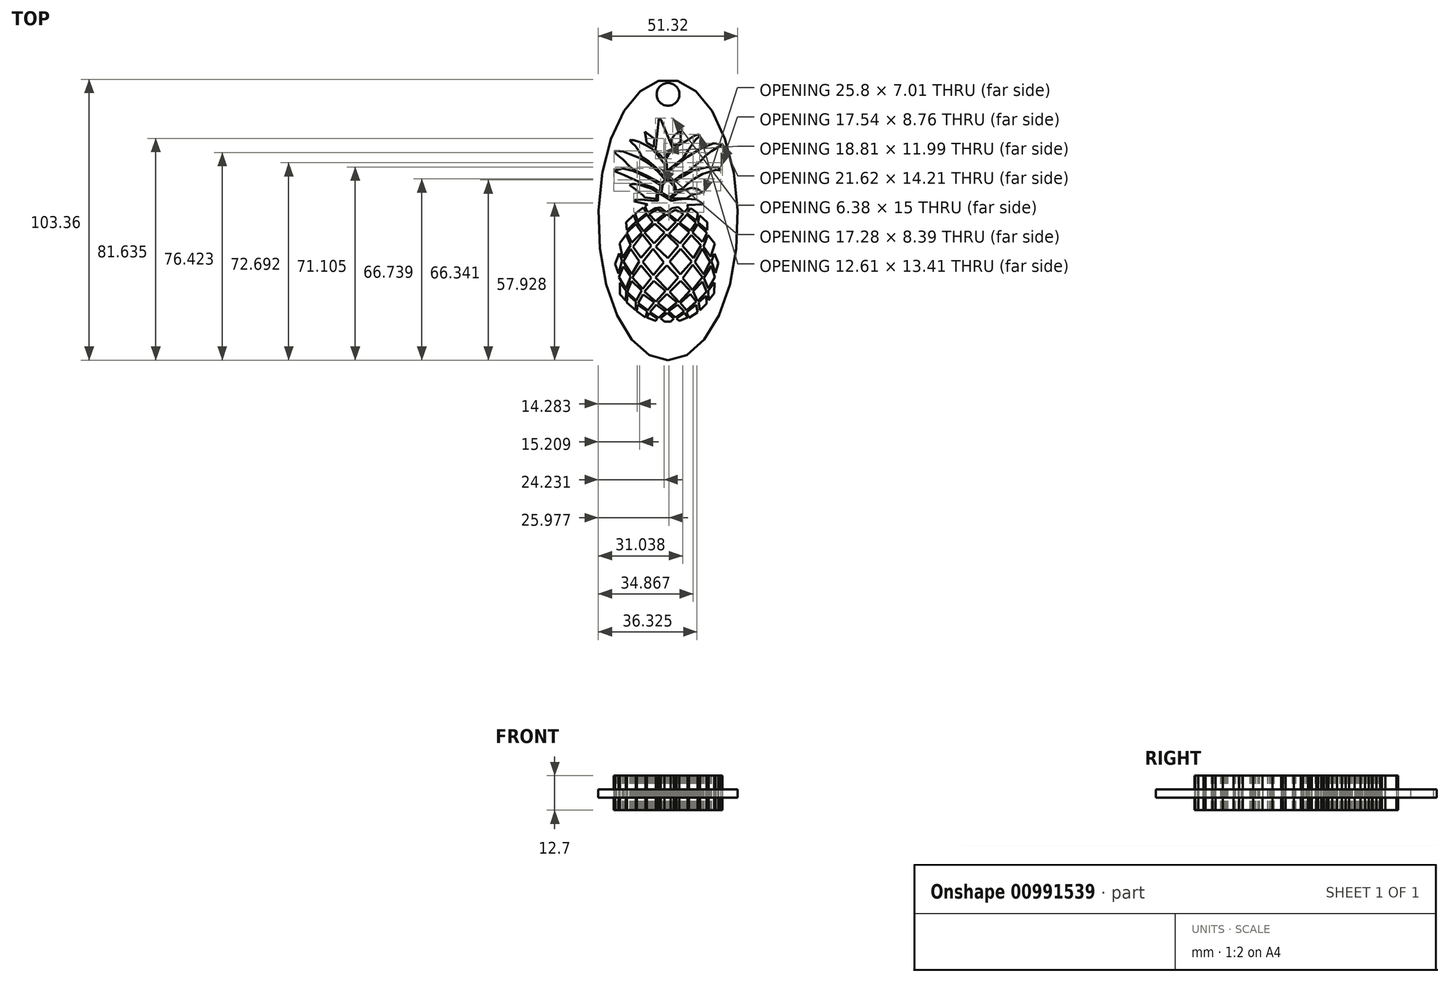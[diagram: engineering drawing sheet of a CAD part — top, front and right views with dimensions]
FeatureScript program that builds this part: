
annotation { "Feature Type Name" : "Feature", "Feature Type Description" : "" }
export const myFeature = defineFeature(function(context is Context, id is Id, definition is map)
    precondition{}
    {
        {
            var Q0;
            Q0=qCreatedBy(makeId("Top.planeOp"),FACE);
            var sketch = newSketch(context, id + "F0", { "sketchPlane" : qUnion([Q0])});
            skLineSegment(sketch, "E0", {"start": v(-25.66, -1.5) * mm, "end": v(-25.25, -6.5) * mm});
            skLineSegment(sketch, "E1", {"start": v(-25.25, -6.5) * mm, "end": v(-19.48, -1.16) * mm});
            skLineSegment(sketch, "E2", {"start": v(-19.48, -1.16) * mm, "end": v(-21, 2.9) * mm});
            skLineSegment(sketch, "E3", {"start": v(-21, 2.9) * mm, "end": v(-25.66, -1.5) * mm});
            skLineSegment(sketch, "E4", {"start": v(-20.22, 3.8) * mm, "end": v(-18.77, -0.42) * mm});
            skLineSegment(sketch, "E5", {"start": v(-18.77, -0.42) * mm, "end": v(-13.06, 4.15) * mm});
            skLineSegment(sketch, "E6", {"start": v(-13.06, 4.15) * mm, "end": v(-15.05, 7.52) * mm});
            skLineSegment(sketch, "E7", {"start": v(-15.05, 7.52) * mm, "end": v(-20.22, 3.8) * mm});
            skLineSegment(sketch, "E8", {"start": v(-18.89, -1.52) * mm, "end": v(-14.98, -7.06) * mm});
            skLineSegment(sketch, "E9", {"start": v(-14.98, -7.06) * mm, "end": v(-9.4, -1.52) * mm});
            skLineSegment(sketch, "E10", {"start": v(-9.4, -1.52) * mm, "end": v(-13.06, 3.14) * mm});
            skLineSegment(sketch, "E11", {"start": v(-13.06, 3.14) * mm, "end": v(-18.89, -1.52) * mm});
            skLineSegment(sketch, "E12", {"start": v(-25.2, -7.88) * mm, "end": v(-22.35, -14.06) * mm});
            skLineSegment(sketch, "E13", {"start": v(-22.35, -14.06) * mm, "end": v(-16.27, -7.88) * mm});
            skLineSegment(sketch, "E14", {"start": v(-16.27, -7.88) * mm, "end": v(-19.8, -2.51) * mm});
            skLineSegment(sketch, "E15", {"start": v(-19.8, -2.51) * mm, "end": v(-25.2, -7.88) * mm});
            skLineSegment(sketch, "E16", {"start": v(-25.66, -9.17) * mm, "end": v(-29.74, -14.43) * mm});
            skLineSegment(sketch, "E17", {"start": v(-29.74, -14.43) * mm, "end": v(-27.7, -23.26) * mm});
            skLineSegment(sketch, "E18", {"start": v(-27.7, -23.26) * mm, "end": v(-22.9, -15.5) * mm});
            skLineSegment(sketch, "E19", {"start": v(-22.9, -15.5) * mm, "end": v(-25.66, -9.17) * mm});
            skLineSegment(sketch, "E20", {"start": v(-21.48, -16.47) * mm, "end": v(-16.64, -23.26) * mm});
            skLineSegment(sketch, "E21", {"start": v(-16.64, -23.26) * mm, "end": v(-10.19, -16.03) * mm});
            skLineSegment(sketch, "E22", {"start": v(-10.19, -16.03) * mm, "end": v(-15.65, -8.87) * mm});
            skLineSegment(sketch, "E23", {"start": v(-15.65, -8.87) * mm, "end": v(-21.48, -16.47) * mm});
            skLineSegment(sketch, "E24", {"start": v(-30, -20.49) * mm, "end": v(-32.38, -27.19) * mm});
            skLineSegment(sketch, "E25", {"start": v(-32.38, -27.19) * mm, "end": v(-30.27, -33.09) * mm});
            skLineSegment(sketch, "E26", {"start": v(-30.27, -33.09) * mm, "end": v(-28.16, -24.99) * mm});
            skLineSegment(sketch, "E27", {"start": v(-28.16, -24.99) * mm, "end": v(-30, -20.49) * mm});
            skLineSegment(sketch, "E28", {"start": v(-27.43, -25.7) * mm, "end": v(-22.9, -17.8) * mm});
            skLineSegment(sketch, "E29", {"start": v(-22.9, -17.8) * mm, "end": v(-17.62, -25.44) * mm});
            skLineSegment(sketch, "E30", {"start": v(-17.62, -25.44) * mm, "end": v(-22.3, -33.55) * mm});
            skLineSegment(sketch, "E31", {"start": v(-22.3, -33.55) * mm, "end": v(-27.43, -25.7) * mm});
            skLineSegment(sketch, "E32", {"start": v(-29.58, -38.67) * mm, "end": v(-25.77, -43.74) * mm});
            skLineSegment(sketch, "E33", {"start": v(-25.77, -43.74) * mm, "end": v(-25.9, -49.5) * mm});
            skLineSegment(sketch, "E34", {"start": v(-25.9, -49.5) * mm, "end": v(-29.58, -45.83) * mm});
            skLineSegment(sketch, "E35", {"start": v(-29.58, -45.83) * mm, "end": v(-29.58, -38.67) * mm});
            skLineSegment(sketch, "E36", {"start": v(-25.89, -42.39) * mm, "end": v(-22.9, -35.09) * mm});
            skLineSegment(sketch, "E37", {"start": v(-22.9, -35.09) * mm, "end": v(-27.43, -28.61) * mm});
            skLineSegment(sketch, "E38", {"start": v(-27.43, -28.61) * mm, "end": v(-30.13, -35.18) * mm});
            skLineSegment(sketch, "E39", {"start": v(-30.13, -35.18) * mm, "end": v(-25.89, -42.39) * mm});
            skLineSegment(sketch, "E40", {"start": v(-25.06, -44.25) * mm, "end": v(-22.28, -37.5) * mm});
            skLineSegment(sketch, "E41", {"start": v(-22.28, -37.5) * mm, "end": v(-16.15, -43.49) * mm});
            skLineSegment(sketch, "E42", {"start": v(-16.15, -43.49) * mm, "end": v(-19.57, -49.5) * mm});
            skLineSegment(sketch, "E43", {"start": v(-19.57, -49.5) * mm, "end": v(-25.06, -44.25) * mm});
            skLineSegment(sketch, "E44", {"start": v(-24.8, -45.83) * mm, "end": v(-19.76, -50.26) * mm});
            skLineSegment(sketch, "E45", {"start": v(-19.76, -50.26) * mm, "end": v(-19.76, -55.47) * mm});
            skLineSegment(sketch, "E46", {"start": v(-19.76, -55.47) * mm, "end": v(-25.36, -50.95) * mm});
            skLineSegment(sketch, "E47", {"start": v(-25.36, -50.95) * mm, "end": v(-24.8, -45.83) * mm});
            skLineSegment(sketch, "E48", {"start": v(-19.16, -56.23) * mm, "end": v(-18.61, -52.19) * mm});
            skLineSegment(sketch, "E49", {"start": v(-18.61, -52.19) * mm, "end": v(-12.83, -56.23) * mm});
            skLineSegment(sketch, "E50", {"start": v(-12.83, -56.23) * mm, "end": v(-13.84, -60) * mm});
            skLineSegment(sketch, "E51", {"start": v(-13.84, -60) * mm, "end": v(-19.16, -56.23) * mm});
            skLineSegment(sketch, "E52", {"start": v(-11.6, -57.29) * mm, "end": v(-6.67, -60.45) * mm});
            skLineSegment(sketch, "E53", {"start": v(-6.67, -60.45) * mm, "end": v(-7.6, -62.06) * mm});
            skLineSegment(sketch, "E54", {"start": v(-7.6, -62.06) * mm, "end": v(-12.92, -60) * mm});
            skLineSegment(sketch, "E55", {"start": v(-12.92, -60) * mm, "end": v(-11.6, -57.29) * mm});
            skLineSegment(sketch, "E56", {"start": v(-2.29, -62.43) * mm, "end": v(1.52, -62.43) * mm});
            skLineSegment(sketch, "E57", {"start": v(1.52, -62.43) * mm, "end": v(3.43, -60.6) * mm});
            skLineSegment(sketch, "E58", {"start": v(3.43, -60.6) * mm, "end": v(-0.54, -57.17) * mm});
            skLineSegment(sketch, "E59", {"start": v(-0.54, -57.17) * mm, "end": v(-4.5, -60.45) * mm});
            skLineSegment(sketch, "E60", {"start": v(-4.5, -60.45) * mm, "end": v(-2.29, -62.43) * mm});
            skLineSegment(sketch, "E61", {"start": v(-5.7, -60.25) * mm, "end": v(-1.49, -56.3) * mm});
            skLineSegment(sketch, "E62", {"start": v(-1.49, -56.3) * mm, "end": v(-7.34, -52.19) * mm});
            skLineSegment(sketch, "E63", {"start": v(-7.34, -52.19) * mm, "end": v(-11.06, -56.55) * mm});
            skLineSegment(sketch, "E64", {"start": v(-11.06, -56.55) * mm, "end": v(-5.7, -60.25) * mm});
            skLineSegment(sketch, "E65", {"start": v(6.85, -62.06) * mm, "end": v(11.9, -60) * mm});
            skLineSegment(sketch, "E66", {"start": v(11.9, -60) * mm, "end": v(10.08, -57.17) * mm});
            skLineSegment(sketch, "E67", {"start": v(10.08, -57.17) * mm, "end": v(5.15, -60.68) * mm});
            skLineSegment(sketch, "E68", {"start": v(5.15, -60.68) * mm, "end": v(6.85, -62.06) * mm});
            skLineSegment(sketch, "E69", {"start": v(4.67, -60) * mm, "end": v(9.8, -56.22) * mm});
            skLineSegment(sketch, "E70", {"start": v(9.8, -56.22) * mm, "end": v(5.95, -52.19) * mm});
            skLineSegment(sketch, "E71", {"start": v(0.4, -56.22) * mm, "end": v(4.67, -60) * mm});
            skLineSegment(sketch, "E72", {"start": v(12.93, -60.09) * mm, "end": v(18.23, -56.83) * mm});
            skLineSegment(sketch, "E73", {"start": v(18.23, -56.83) * mm, "end": v(17.22, -52.19) * mm});
            skLineSegment(sketch, "E74", {"start": v(17.22, -52.19) * mm, "end": v(11.26, -56.78) * mm});
            skLineSegment(sketch, "E75", {"start": v(11.26, -56.78) * mm, "end": v(12.93, -60.09) * mm});
            skLineSegment(sketch, "E76", {"start": v(19.52, -55.6) * mm, "end": v(23.67, -51.43) * mm});
            skLineSegment(sketch, "E77", {"start": v(23.67, -51.43) * mm, "end": v(23.5, -46.61) * mm});
            skLineSegment(sketch, "E78", {"start": v(23.5, -46.61) * mm, "end": v(18.83, -50.6) * mm});
            skLineSegment(sketch, "E79", {"start": v(18.83, -50.6) * mm, "end": v(19.52, -55.6) * mm});
            skLineSegment(sketch, "E80", {"start": v(24.87, -49.48) * mm, "end": v(28.22, -45.16) * mm});
            skLineSegment(sketch, "E81", {"start": v(28.22, -45.16) * mm, "end": v(28.52, -38.53) * mm});
            skLineSegment(sketch, "E82", {"start": v(28.52, -38.53) * mm, "end": v(24.7, -43.42) * mm});
            skLineSegment(sketch, "E83", {"start": v(24.7, -43.42) * mm, "end": v(24.87, -49.48) * mm});
            skLineSegment(sketch, "E84", {"start": v(24.7, -42.23) * mm, "end": v(28.81, -35.16) * mm});
            skLineSegment(sketch, "E85", {"start": v(28.81, -35.16) * mm, "end": v(26.61, -28.25) * mm});
            skLineSegment(sketch, "E86", {"start": v(26.61, -28.25) * mm, "end": v(21.88, -35.61) * mm});
            skLineSegment(sketch, "E87", {"start": v(21.88, -35.61) * mm, "end": v(24.7, -42.23) * mm});
            skLineSegment(sketch, "E88", {"start": v(29.1, -32.7) * mm, "end": v(30.74, -26.55) * mm});
            skLineSegment(sketch, "E89", {"start": v(30.74, -26.55) * mm, "end": v(28.5, -20.78) * mm});
            skLineSegment(sketch, "E90", {"start": v(28.5, -20.78) * mm, "end": v(26.59, -25.37) * mm});
            skLineSegment(sketch, "E91", {"start": v(26.59, -25.37) * mm, "end": v(29.1, -32.7) * mm});
            skLineSegment(sketch, "E92", {"start": v(26.08, -22.69) * mm, "end": v(28.81, -14.65) * mm});
            skLineSegment(sketch, "E93", {"start": v(28.81, -14.65) * mm, "end": v(24.54, -9.28) * mm});
            skLineSegment(sketch, "E94", {"start": v(24.54, -9.28) * mm, "end": v(21.68, -16.37) * mm});
            skLineSegment(sketch, "E95", {"start": v(21.68, -16.37) * mm, "end": v(26.08, -22.69) * mm});
            skLineSegment(sketch, "E96", {"start": v(20.99, -13.69) * mm, "end": v(23.83, -8.2) * mm});
            skLineSegment(sketch, "E97", {"start": v(23.83, -8.2) * mm, "end": v(18.2, -2.6) * mm});
            skLineSegment(sketch, "E98", {"start": v(18.2, -2.6) * mm, "end": v(14.88, -7.74) * mm});
            skLineSegment(sketch, "E99", {"start": v(14.88, -7.74) * mm, "end": v(20.99, -13.69) * mm});
            skLineSegment(sketch, "E100", {"start": v(24.02, -6.48) * mm, "end": v(24.02, -1.54) * mm});
            skLineSegment(sketch, "E101", {"start": v(24.02, -1.54) * mm, "end": v(19.36, 2.68) * mm});
            skLineSegment(sketch, "E102", {"start": v(19.36, 2.68) * mm, "end": v(18.28, -1.59) * mm});
            skLineSegment(sketch, "E103", {"start": v(18.28, -1.59) * mm, "end": v(24.02, -6.48) * mm});
            skLineSegment(sketch, "E104", {"start": v(11.46, 3.92) * mm, "end": v(13.8, 7.2) * mm});
            skLineSegment(sketch, "E105", {"start": v(13.8, 7.2) * mm, "end": v(18.28, 3.92) * mm});
            skLineSegment(sketch, "E106", {"start": v(18.28, 3.92) * mm, "end": v(17.48, -0.47) * mm});
            skLineSegment(sketch, "E107", {"start": v(17.48, -0.47) * mm, "end": v(11.46, 3.92) * mm});
            skLineSegment(sketch, "E108", {"start": v(5.77, -0.72) * mm, "end": v(9.53, 3.67) * mm});
            skLineSegment(sketch, "E109", {"start": v(9.53, 3.67) * mm, "end": v(4.63, 6.14) * mm});
            skLineSegment(sketch, "E110", {"start": v(4.63, 6.14) * mm, "end": v(0.21, 3.76) * mm});
            skLineSegment(sketch, "E111", {"start": v(0.21, 3.76) * mm, "end": v(5.77, -0.72) * mm});
            skLineSegment(sketch, "E112", {"start": v(7.17, -1.68) * mm, "end": v(13.64, -6.64) * mm});
            skLineSegment(sketch, "E113", {"start": v(13.64, -6.64) * mm, "end": v(16.97, -1.68) * mm});
            skLineSegment(sketch, "E114", {"start": v(16.97, -1.68) * mm, "end": v(11.46, 3.12) * mm});
            skLineSegment(sketch, "E115", {"start": v(11.46, 3.12) * mm, "end": v(7.17, -1.68) * mm});
            skLineSegment(sketch, "E116", {"start": v(-11.65, 3.55) * mm, "end": v(-6.31, 6.44) * mm});
            skLineSegment(sketch, "E117", {"start": v(-6.31, 6.44) * mm, "end": v(-2.07, 3.81) * mm});
            skLineSegment(sketch, "E118", {"start": v(-2.07, 3.81) * mm, "end": v(-7.74, -0.72) * mm});
            skLineSegment(sketch, "E119", {"start": v(-7.74, -0.72) * mm, "end": v(-11.65, 3.55) * mm});
            skLineSegment(sketch, "E120", {"start": v(-14.43, -7.97) * mm, "end": v(-8.05, -2.34) * mm});
            skLineSegment(sketch, "E121", {"start": v(-8.05, -2.34) * mm, "end": v(-2.26, -7.97) * mm});
            skLineSegment(sketch, "E122", {"start": v(-2.26, -7.97) * mm, "end": v(-8.44, -14.46) * mm});
            skLineSegment(sketch, "E123", {"start": v(-8.44, -14.46) * mm, "end": v(-14.43, -7.97) * mm});
            skLineSegment(sketch, "E124", {"start": v(-6.53, -1.28) * mm, "end": v(-0.6, -6.64) * mm});
            skLineSegment(sketch, "E125", {"start": v(-0.6, -6.64) * mm, "end": v(4.87, -1.4) * mm});
            skLineSegment(sketch, "E126", {"start": v(4.87, -1.4) * mm, "end": v(-0.73, 3.37) * mm});
            skLineSegment(sketch, "E127", {"start": v(-0.73, 3.37) * mm, "end": v(-6.53, -1.28) * mm});
            skLineSegment(sketch, "E128", {"start": v(0.58, -8.69) * mm, "end": v(7.43, -14.46) * mm});
            skLineSegment(sketch, "E129", {"start": v(7.43, -14.46) * mm, "end": v(13.07, -7.72) * mm});
            skLineSegment(sketch, "E130", {"start": v(13.07, -7.72) * mm, "end": v(6.52, -2.19) * mm});
            skLineSegment(sketch, "E131", {"start": v(6.52, -2.19) * mm, "end": v(0.58, -8.69) * mm});
            skLineSegment(sketch, "E132", {"start": v(-7.39, -16.48) * mm, "end": v(-0.83, -8.87) * mm});
            skLineSegment(sketch, "E133", {"start": v(-0.83, -8.87) * mm, "end": v(6.37, -15.98) * mm});
            skLineSegment(sketch, "E134", {"start": v(6.37, -15.98) * mm, "end": v(0.02, -23.62) * mm});
            skLineSegment(sketch, "E135", {"start": v(0.02, -23.62) * mm, "end": v(-7.39, -16.48) * mm});
            skLineSegment(sketch, "E136", {"start": v(8.75, -15.98) * mm, "end": v(14.4, -9.28) * mm});
            skLineSegment(sketch, "E137", {"start": v(14.4, -9.28) * mm, "end": v(20.16, -15.77) * mm});
            skLineSegment(sketch, "E138", {"start": v(20.16, -15.77) * mm, "end": v(15.51, -23.62) * mm});
            skLineSegment(sketch, "E139", {"start": v(15.51, -23.62) * mm, "end": v(8.75, -15.98) * mm});
            skLineSegment(sketch, "E140", {"start": v(16.38, -25.9) * mm, "end": v(21.15, -17.57) * mm});
            skLineSegment(sketch, "E141", {"start": v(21.15, -17.57) * mm, "end": v(25.73, -25.67) * mm});
            skLineSegment(sketch, "E142", {"start": v(25.73, -25.67) * mm, "end": v(21.88, -33.55) * mm});
            skLineSegment(sketch, "E143", {"start": v(21.88, -33.55) * mm, "end": v(16.38, -25.9) * mm});
            skLineSegment(sketch, "E144", {"start": v(7.56, -33.55) * mm, "end": v(14.46, -25.67) * mm});
            skLineSegment(sketch, "E145", {"start": v(14.46, -25.67) * mm, "end": v(7.74, -17.8) * mm});
            skLineSegment(sketch, "E146", {"start": v(7.74, -17.8) * mm, "end": v(0.95, -25.67) * mm});
            skLineSegment(sketch, "E147", {"start": v(0.95, -25.67) * mm, "end": v(7.56, -33.55) * mm});
            skLineSegment(sketch, "E148", {"start": v(8.97, -35.82) * mm, "end": v(15.15, -27.62) * mm});
            skLineSegment(sketch, "E149", {"start": v(15.15, -27.62) * mm, "end": v(21.06, -35.24) * mm});
            skLineSegment(sketch, "E150", {"start": v(21.06, -35.24) * mm, "end": v(14.88, -43.05) * mm});
            skLineSegment(sketch, "E151", {"start": v(14.88, -43.05) * mm, "end": v(8.97, -35.82) * mm});
            skLineSegment(sketch, "E152", {"start": v(-8.93, -33.88) * mm, "end": v(-2.54, -26.12) * mm});
            skLineSegment(sketch, "E153", {"start": v(-2.54, -26.12) * mm, "end": v(-9.24, -17.8) * mm});
            skLineSegment(sketch, "E154", {"start": v(-9.24, -17.8) * mm, "end": v(-15.59, -25.84) * mm});
            skLineSegment(sketch, "E155", {"start": v(-15.59, -25.84) * mm, "end": v(-8.93, -33.88) * mm});
            skLineSegment(sketch, "E156", {"start": v(-21.8, -35.5) * mm, "end": v(-16.7, -27.93) * mm});
            skLineSegment(sketch, "E157", {"start": v(-16.7, -27.93) * mm, "end": v(-10.19, -35.65) * mm});
            skLineSegment(sketch, "E158", {"start": v(-10.19, -35.65) * mm, "end": v(-15.59, -42.39) * mm});
            skLineSegment(sketch, "E159", {"start": v(-15.59, -42.39) * mm, "end": v(-21.8, -35.5) * mm});
            skLineSegment(sketch, "E160", {"start": v(-7.65, -35.5) * mm, "end": v(-0.2, -43.05) * mm});
            skLineSegment(sketch, "E161", {"start": v(-0.2, -43.05) * mm, "end": v(6.37, -35.5) * mm});
            skLineSegment(sketch, "E162", {"start": v(6.37, -35.5) * mm, "end": v(-0.64, -27.93) * mm});
            skLineSegment(sketch, "E163", {"start": v(-14.49, -44.08) * mm, "end": v(-8.75, -37.5) * mm});
            skLineSegment(sketch, "E164", {"start": v(-8.75, -37.5) * mm, "end": v(-1.49, -43.71) * mm});
            skLineSegment(sketch, "E165", {"start": v(-1.49, -43.71) * mm, "end": v(-7.39, -50.2) * mm});
            skLineSegment(sketch, "E166", {"start": v(-7.39, -50.2) * mm, "end": v(-14.49, -44.08) * mm});
            skLineSegment(sketch, "E167", {"start": v(-18.32, -51.11) * mm, "end": v(-15.37, -45.83) * mm});
            skLineSegment(sketch, "E168", {"start": v(-15.37, -45.83) * mm, "end": v(-8.49, -50.65) * mm});
            skLineSegment(sketch, "E169", {"start": v(-8.49, -50.65) * mm, "end": v(-12.41, -55.6) * mm});
            skLineSegment(sketch, "E170", {"start": v(-12.41, -55.6) * mm, "end": v(-18.32, -51.11) * mm});
            skLineSegment(sketch, "E171", {"start": v(-6.27, -51.11) * mm, "end": v(-0.64, -45.48) * mm});
            skLineSegment(sketch, "E172", {"start": v(-0.64, -45.48) * mm, "end": v(5.45, -50.72) * mm});
            skLineSegment(sketch, "E173", {"start": v(5.45, -50.72) * mm, "end": v(-0.41, -55.6) * mm});
            skLineSegment(sketch, "E174", {"start": v(-0.41, -55.6) * mm, "end": v(-6.27, -51.11) * mm});
            skLineSegment(sketch, "E175", {"start": v(0.95, -44.29) * mm, "end": v(7.7, -37.5) * mm});
            skLineSegment(sketch, "E176", {"start": v(7.7, -37.5) * mm, "end": v(13.43, -43.5) * mm});
            skLineSegment(sketch, "E177", {"start": v(13.43, -43.5) * mm, "end": v(6.95, -50.54) * mm});
            skLineSegment(sketch, "E178", {"start": v(6.95, -50.54) * mm, "end": v(0.95, -44.29) * mm});
            skLineSegment(sketch, "E179", {"start": v(7.47, -51.11) * mm, "end": v(13.7, -45.48) * mm});
            skLineSegment(sketch, "E180", {"start": v(13.7, -45.48) * mm, "end": v(17.35, -50.2) * mm});
            skLineSegment(sketch, "E181", {"start": v(17.35, -50.2) * mm, "end": v(11.26, -55.6) * mm});
            skLineSegment(sketch, "E182", {"start": v(11.26, -55.6) * mm, "end": v(7.47, -51.11) * mm});
            skLineSegment(sketch, "E183", {"start": v(15.32, -43.85) * mm, "end": v(18.23, -49.93) * mm});
            skLineSegment(sketch, "E184", {"start": v(18.23, -49.93) * mm, "end": v(23.67, -44.08) * mm});
            skLineSegment(sketch, "E185", {"start": v(23.67, -44.08) * mm, "end": v(21.06, -37.85) * mm});
            skLineSegment(sketch, "E186", {"start": v(21.06, -37.85) * mm, "end": v(15.32, -43.85) * mm});
            skLineSegment(sketch, "E187", {"start": v(-0.83, 4.57) * mm, "end": v(2.5, 7.2) * mm});
            skLineSegment(sketch, "E188", {"start": v(2.5, 7.2) * mm, "end": v(6.37, 7.8) * mm});
            skLineSegment(sketch, "E189", {"start": v(6.37, 7.8) * mm, "end": v(9.9, 4.57) * mm});
            skLineSegment(sketch, "E190", {"start": v(9.9, 4.57) * mm, "end": v(11.62, 6.2) * mm});
            skLineSegment(sketch, "E191", {"start": v(11.62, 6.2) * mm, "end": v(12.33, 7.83) * mm});
            skLineSegment(sketch, "E192", {"start": v(12.33, 7.83) * mm, "end": v(11.46, 9.03) * mm});
            skLineSegment(sketch, "E193", {"start": v(11.46, 9.03) * mm, "end": v(22.03, 9.55) * mm});
            skLineSegment(sketch, "E194", {"start": v(22.03, 9.55) * mm, "end": v(17.4, 12.38) * mm});
            skLineSegment(sketch, "E195", {"start": v(17.4, 12.38) * mm, "end": v(11, 12.77) * mm});
            skLineSegment(sketch, "E196", {"start": v(11, 12.77) * mm, "end": v(6.02, 12.42) * mm});
            skLineSegment(sketch, "E197", {"start": v(6.02, 12.42) * mm, "end": v(2.27, 11.63) * mm});
            skLineSegment(sketch, "E198", {"start": v(2.27, 11.63) * mm, "end": v(-5.18, 16.26) * mm});
            skLineSegment(sketch, "E199", {"start": v(-5.18, 16.26) * mm, "end": v(-6.15, 15.07) * mm});
            skLineSegment(sketch, "E200", {"start": v(-6.15, 15.07) * mm, "end": v(-6.15, 11.58) * mm});
            skLineSegment(sketch, "E201", {"start": v(-6.15, 11.58) * mm, "end": v(-10.37, 11.86) * mm});
            skLineSegment(sketch, "E202", {"start": v(-10.37, 11.86) * mm, "end": v(-16.64, 12.47) * mm});
            skLineSegment(sketch, "E203", {"start": v(-16.64, 12.47) * mm, "end": v(-20.48, 12.16) * mm});
            skLineSegment(sketch, "E204", {"start": v(-20.48, 12.16) * mm, "end": v(-20.97, 11.4) * mm});
            skLineSegment(sketch, "E205", {"start": v(-20.97, 11.4) * mm, "end": v(-12.59, 9.51) * mm});
            skLineSegment(sketch, "E206", {"start": v(-12.59, 9.51) * mm, "end": v(-14.15, 8.1) * mm});
            skLineSegment(sketch, "E207", {"start": v(-14.15, 8.1) * mm, "end": v(-13.25, 5.8) * mm});
            skLineSegment(sketch, "E208", {"start": v(-13.25, 5.8) * mm, "end": v(-11.65, 4.57) * mm});
            skLineSegment(sketch, "E209", {"start": v(-11.65, 4.57) * mm, "end": v(-7.78, 7.2) * mm});
            skLineSegment(sketch, "E210", {"start": v(-7.78, 7.2) * mm, "end": v(-4.65, 7.52) * mm});
            skLineSegment(sketch, "E211", {"start": v(-4.65, 7.52) * mm, "end": v(-0.83, 4.57) * mm});
            skLineSegment(sketch, "E212", {"start": v(1.74, 13.08) * mm, "end": v(11.46, 13.3) * mm});
            skLineSegment(sketch, "E213", {"start": v(11.46, 13.3) * mm, "end": v(14.46, 15.33) * mm});
            skLineSegment(sketch, "E214", {"start": v(14.46, 15.33) * mm, "end": v(19.36, 16.26) * mm});
            skLineSegment(sketch, "E215", {"start": v(19.36, 16.26) * mm, "end": v(21.15, 16.87) * mm});
            skLineSegment(sketch, "E216", {"start": v(21.15, 16.87) * mm, "end": v(18.28, 18.73) * mm});
            skLineSegment(sketch, "E217", {"start": v(18.28, 18.73) * mm, "end": v(14.46, 19.65) * mm});
            skLineSegment(sketch, "E218", {"start": v(14.46, 19.65) * mm, "end": v(9.63, 18.18) * mm});
            skLineSegment(sketch, "E219", {"start": v(9.63, 18.18) * mm, "end": v(6.1, 16.66) * mm});
            skLineSegment(sketch, "E220", {"start": v(6.1, 16.66) * mm, "end": v(1.74, 13.08) * mm});
            skLineSegment(sketch, "E221", {"start": v(-23.48, 21.37) * mm, "end": v(-19.48, 18.33) * mm});
            skLineSegment(sketch, "E222", {"start": v(-19.48, 18.33) * mm, "end": v(-15.37, 14.98) * mm});
            skLineSegment(sketch, "E223", {"start": v(-15.37, 14.98) * mm, "end": v(-14.21, 13.6) * mm});
            skLineSegment(sketch, "E224", {"start": v(-14.21, 13.6) * mm, "end": v(-7.17, 12.86) * mm});
            skLineSegment(sketch, "E225", {"start": v(-7.17, 12.86) * mm, "end": v(-7.17, 14.85) * mm});
            skLineSegment(sketch, "E226", {"start": v(-7.17, 14.85) * mm, "end": v(-6.53, 16.79) * mm});
            skLineSegment(sketch, "E227", {"start": v(-6.53, 16.79) * mm, "end": v(-9.74, 19) * mm});
            skLineSegment(sketch, "E228", {"start": v(-9.74, 19) * mm, "end": v(-19.12, 22) * mm});
            skLineSegment(sketch, "E229", {"start": v(-19.12, 22) * mm, "end": v(-21.98, 22) * mm});
            skLineSegment(sketch, "E230", {"start": v(-21.98, 22) * mm, "end": v(-23.48, 21.37) * mm});
            skLineSegment(sketch, "E231", {"start": v(-4.08, 16.61) * mm, "end": v(0.95, 13.79) * mm});
            skLineSegment(sketch, "E232", {"start": v(0.95, 13.79) * mm, "end": v(4.65, 16.96) * mm});
            skLineSegment(sketch, "E233", {"start": v(4.65, 16.96) * mm, "end": v(3.6, 20.78) * mm});
            skLineSegment(sketch, "E234", {"start": v(3.6, 20.78) * mm, "end": v(-0.1, 24.61) * mm});
            skLineSegment(sketch, "E235", {"start": v(-0.1, 24.61) * mm, "end": v(-3.27, 21.5) * mm});
            skLineSegment(sketch, "E236", {"start": v(-3.27, 21.5) * mm, "end": v(-4.08, 16.61) * mm});
            skLineSegment(sketch, "E237", {"start": v(-33.36, 29.93) * mm, "end": v(-26.88, 27.46) * mm});
            skLineSegment(sketch, "E238", {"start": v(-26.88, 27.46) * mm, "end": v(-21.85, 25.2) * mm});
            skLineSegment(sketch, "E239", {"start": v(-21.85, 25.2) * mm, "end": v(-17, 22.92) * mm});
            skLineSegment(sketch, "E240", {"start": v(-17, 22.92) * mm, "end": v(-15, 21.64) * mm});
            skLineSegment(sketch, "E241", {"start": v(-11.65, 20.71) * mm, "end": v(-8.8, 19.65) * mm});
            skLineSegment(sketch, "E242", {"start": v(-8.8, 19.65) * mm, "end": v(-6.86, 18.42) * mm});
            skLineSegment(sketch, "E243", {"start": v(-6.86, 18.42) * mm, "end": v(-6.33, 17.44) * mm});
            skLineSegment(sketch, "E244", {"start": v(-6.33, 17.44) * mm, "end": v(-4.96, 17.44) * mm});
            skLineSegment(sketch, "E245", {"start": v(-4.96, 17.44) * mm, "end": v(-4.65, 20.05) * mm});
            skLineSegment(sketch, "E246", {"start": v(-4.65, 20.05) * mm, "end": v(-4.56, 21.36) * mm});
            skLineSegment(sketch, "E247", {"start": v(-4.56, 21.36) * mm, "end": v(-7.65, 23.31) * mm});
            skLineSegment(sketch, "E248", {"start": v(-7.65, 23.31) * mm, "end": v(-14.15, 26.58) * mm});
            skLineSegment(sketch, "E249", {"start": v(-14.15, 26.58) * mm, "end": v(-21.5, 29.93) * mm});
            skLineSegment(sketch, "E250", {"start": v(-21.5, 29.93) * mm, "end": v(-27.76, 31.43) * mm});
            skLineSegment(sketch, "E251", {"start": v(-27.76, 31.43) * mm, "end": v(-33.36, 29.93) * mm});
            skLineSegment(sketch, "E252", {"start": v(5.14, 17.8) * mm, "end": v(9.06, 19.26) * mm});
            skLineSegment(sketch, "E253", {"start": v(9.06, 19.26) * mm, "end": v(11.7, 22.02) * mm});
            skLineSegment(sketch, "E254", {"start": v(11.7, 22.02) * mm, "end": v(16.03, 25.08) * mm});
            skLineSegment(sketch, "E255", {"start": v(16.03, 25.08) * mm, "end": v(21.15, 27.99) * mm});
            skLineSegment(sketch, "E256", {"start": v(21.15, 27.99) * mm, "end": v(29.3, 30.68) * mm});
            skLineSegment(sketch, "E257", {"start": v(29.3, 30.68) * mm, "end": v(32.39, 30.24) * mm});
            skLineSegment(sketch, "E258", {"start": v(32.39, 30.24) * mm, "end": v(30.93, 32.4) * mm});
            skLineSegment(sketch, "E259", {"start": v(30.93, 32.4) * mm, "end": v(23.13, 32.04) * mm});
            skLineSegment(sketch, "E260", {"start": v(23.13, 32.04) * mm, "end": v(15.2, 30.1) * mm});
            skLineSegment(sketch, "E261", {"start": v(15.2, 30.1) * mm, "end": v(8.67, 26.46) * mm});
            skLineSegment(sketch, "E262", {"start": v(8.67, 26.46) * mm, "end": v(3.16, 22.61) * mm});
            skLineSegment(sketch, "E263", {"start": v(3.16, 22.61) * mm, "end": v(4.21, 21.06) * mm});
            skLineSegment(sketch, "E264", {"start": v(4.21, 21.06) * mm, "end": v(5.14, 17.8) * mm});
            skLineSegment(sketch, "E265", {"start": v(-4.08, 22.39) * mm, "end": v(-1.74, 24.43) * mm});
            skLineSegment(sketch, "E266", {"start": v(-1.74, 24.43) * mm, "end": v(-5.76, 29.08) * mm});
            skLineSegment(sketch, "E267", {"start": v(-5.76, 29.08) * mm, "end": v(-10.38, 33.28) * mm});
            skLineSegment(sketch, "E268", {"start": v(-10.38, 33.28) * mm, "end": v(-14.53, 36.23) * mm});
            skLineSegment(sketch, "E269", {"start": v(-14.53, 36.23) * mm, "end": v(-18.28, 38.22) * mm});
            skLineSegment(sketch, "E270", {"start": v(-18.28, 38.22) * mm, "end": v(-23.22, 40.07) * mm});
            skLineSegment(sketch, "E271", {"start": v(-23.22, 40.07) * mm, "end": v(-27.32, 41.75) * mm});
            skLineSegment(sketch, "E272", {"start": v(-27.32, 41.75) * mm, "end": v(-31.55, 42.36) * mm});
            skLineSegment(sketch, "E273", {"start": v(-31.55, 42.36) * mm, "end": v(-33.1, 42.1) * mm});
            skLineSegment(sketch, "E274", {"start": v(-33.1, 42.1) * mm, "end": v(-31.82, 40.3) * mm});
            skLineSegment(sketch, "E275", {"start": v(-31.82, 40.3) * mm, "end": v(-27.54, 37.03) * mm});
            skLineSegment(sketch, "E276", {"start": v(-27.54, 37.03) * mm, "end": v(-23.48, 32.8) * mm});
            skLineSegment(sketch, "E277", {"start": v(-23.48, 32.8) * mm, "end": v(-20.84, 30.54) * mm});
            skLineSegment(sketch, "E278", {"start": v(-20.84, 30.54) * mm, "end": v(-12.99, 27.06) * mm});
            skLineSegment(sketch, "E279", {"start": v(-12.99, 27.06) * mm, "end": v(-4.08, 22.39) * mm});
            skLineSegment(sketch, "E280", {"start": v(-3.33, 27.24) * mm, "end": v(-1.43, 29.13) * mm});
            skLineSegment(sketch, "E281", {"start": v(-1.43, 29.13) * mm, "end": v(-2.2, 34.34) * mm});
            skLineSegment(sketch, "E282", {"start": v(-2.2, 34.34) * mm, "end": v(-6.55, 39.96) * mm});
            skLineSegment(sketch, "E283", {"start": v(-6.55, 39.96) * mm, "end": v(-10.03, 43.69) * mm});
            skLineSegment(sketch, "E284", {"start": v(-10.03, 43.69) * mm, "end": v(-13.43, 45.67) * mm});
            skLineSegment(sketch, "E285", {"start": v(-13.43, 45.67) * mm, "end": v(-17.62, 47.83) * mm});
            skLineSegment(sketch, "E286", {"start": v(-17.62, 47.83) * mm, "end": v(-21.05, 48.93) * mm});
            skLineSegment(sketch, "E287", {"start": v(-21.05, 48.93) * mm, "end": v(-23.48, 48.93) * mm});
            skLineSegment(sketch, "E288", {"start": v(-23.48, 48.93) * mm, "end": v(-22.11, 47.21) * mm});
            skLineSegment(sketch, "E289", {"start": v(-22.11, 47.21) * mm, "end": v(-19.95, 45.23) * mm});
            skLineSegment(sketch, "E290", {"start": v(-19.95, 45.23) * mm, "end": v(-18.01, 42.38) * mm});
            skLineSegment(sketch, "E291", {"start": v(-18.01, 42.38) * mm, "end": v(-15.94, 38.48) * mm});
            skLineSegment(sketch, "E292", {"start": v(-15.94, 38.48) * mm, "end": v(-11.75, 35.75) * mm});
            skLineSegment(sketch, "E293", {"start": v(-11.75, 35.75) * mm, "end": v(-7.43, 32.09) * mm});
            skLineSegment(sketch, "E294", {"start": v(-7.43, 32.09) * mm, "end": v(-3.33, 27.24) * mm});
            skLineSegment(sketch, "E295", {"start": v(-2.67, 26.66) * mm, "end": v(-1.43, 25.1) * mm});
            skLineSegment(sketch, "E296", {"start": v(-1.43, 25.1) * mm, "end": v(0.49, 25.1) * mm});
            skLineSegment(sketch, "E297", {"start": v(0.49, 25.1) * mm, "end": v(1.74, 24.2) * mm});
            skLineSegment(sketch, "E298", {"start": v(1.74, 24.2) * mm, "end": v(2.4, 23.18) * mm});
            skLineSegment(sketch, "E299", {"start": v(2.4, 23.18) * mm, "end": v(4.65, 24.92) * mm});
            skLineSegment(sketch, "E300", {"start": v(4.65, 24.92) * mm, "end": v(6.86, 26.66) * mm});
            skLineSegment(sketch, "E301", {"start": v(6.86, 26.66) * mm, "end": v(10.2, 28.78) * mm});
            skLineSegment(sketch, "E302", {"start": v(10.2, 28.78) * mm, "end": v(12.2, 29.49) * mm});
            skLineSegment(sketch, "E303", {"start": v(12.2, 29.49) * mm, "end": v(19.9, 35.84) * mm});
            skLineSegment(sketch, "E304", {"start": v(19.9, 35.84) * mm, "end": v(23.08, 39.4) * mm});
            skLineSegment(sketch, "E305", {"start": v(23.08, 39.4) * mm, "end": v(26.57, 42.1) * mm});
            skLineSegment(sketch, "E306", {"start": v(26.57, 42.1) * mm, "end": v(30.36, 44.4) * mm});
            skLineSegment(sketch, "E307", {"start": v(30.36, 44.4) * mm, "end": v(33.36, 46.38) * mm});
            skLineSegment(sketch, "E308", {"start": v(33.36, 46.38) * mm, "end": v(27.94, 46.86) * mm});
            skLineSegment(sketch, "E309", {"start": v(27.94, 46.86) * mm, "end": v(19.87, 43.6) * mm});
            skLineSegment(sketch, "E310", {"start": v(19.87, 43.6) * mm, "end": v(12.06, 38.75) * mm});
            skLineSegment(sketch, "E311", {"start": v(12.06, 38.75) * mm, "end": v(4.52, 32.93) * mm});
            skLineSegment(sketch, "E312", {"start": v(4.52, 32.93) * mm, "end": v(0.17, 29.6) * mm});
            skLineSegment(sketch, "E313", {"start": v(0.17, 29.6) * mm, "end": v(-2.67, 26.66) * mm});
            skLineSegment(sketch, "E314", {"start": v(-0.77, 30.06) * mm, "end": v(-0.77, 33.76) * mm});
            skLineSegment(sketch, "E315", {"start": v(-0.77, 33.76) * mm, "end": v(-1.54, 37.02) * mm});
            skLineSegment(sketch, "E316", {"start": v(-1.54, 37.02) * mm, "end": v(0.29, 40.16) * mm});
            skLineSegment(sketch, "E317", {"start": v(0.29, 40.16) * mm, "end": v(2.84, 42.85) * mm});
            skLineSegment(sketch, "E318", {"start": v(2.84, 42.85) * mm, "end": v(5.36, 44.79) * mm});
            skLineSegment(sketch, "E319", {"start": v(5.36, 44.79) * mm, "end": v(8.58, 46.9) * mm});
            skLineSegment(sketch, "E320", {"start": v(8.58, 46.9) * mm, "end": v(11.97, 48.89) * mm});
            skLineSegment(sketch, "E321", {"start": v(11.97, 48.89) * mm, "end": v(14.7, 50.65) * mm});
            skLineSegment(sketch, "E322", {"start": v(14.7, 50.65) * mm, "end": v(16.73, 51.89) * mm});
            skLineSegment(sketch, "E323", {"start": v(16.73, 51.89) * mm, "end": v(18.98, 52.42) * mm});
            skLineSegment(sketch, "E324", {"start": v(18.98, 52.42) * mm, "end": v(19.47, 51.45) * mm});
            skLineSegment(sketch, "E325", {"start": v(19.47, 51.45) * mm, "end": v(16.91, 49.11) * mm});
            skLineSegment(sketch, "E326", {"start": v(16.91, 49.11) * mm, "end": v(14.97, 46.46) * mm});
            skLineSegment(sketch, "E327", {"start": v(14.97, 46.46) * mm, "end": v(12.41, 42.67) * mm});
            skLineSegment(sketch, "E328", {"start": v(12.41, 42.67) * mm, "end": v(9.33, 37.82) * mm});
            skLineSegment(sketch, "E329", {"start": v(9.33, 37.82) * mm, "end": v(-0.77, 30.06) * mm});
            skLineSegment(sketch, "E330", {"start": v(-2.67, 37.42) * mm, "end": v(-0.33, 40.73) * mm});
            skLineSegment(sketch, "E331", {"start": v(-0.33, 40.73) * mm, "end": v(2.93, 44) * mm});
            skLineSegment(sketch, "E332", {"start": v(2.93, 44) * mm, "end": v(-4.39, 61.28) * mm});
            skLineSegment(sketch, "E333", {"start": v(-4.39, 61.28) * mm, "end": v(-5.53, 62.43) * mm});
            skLineSegment(sketch, "E334", {"start": v(-5.53, 62.43) * mm, "end": v(-7.7, 42.9) * mm});
            skLineSegment(sketch, "E335", {"start": v(-7.7, 42.9) * mm, "end": v(-2.67, 37.42) * mm});
            skLineSegment(sketch, "E336", {"start": v(-8.7, 44.88) * mm, "end": v(-8.31, 49.76) * mm});
            skLineSegment(sketch, "E337", {"start": v(-8.31, 49.76) * mm, "end": v(-14.35, 54.1) * mm});
            skLineSegment(sketch, "E338", {"start": v(-14.35, 54.1) * mm, "end": v(-13.43, 49.64) * mm});
            skLineSegment(sketch, "E339", {"start": v(-13.43, 49.64) * mm, "end": v(-13.28, 47.43) * mm});
            skLineSegment(sketch, "E340", {"start": v(-13.28, 47.43) * mm, "end": v(-8.7, 44.88) * mm});
            skLineSegment(sketch, "E341", {"start": v(3.73, 45.15) * mm, "end": v(7.7, 47.96) * mm});
            skLineSegment(sketch, "E342", {"start": v(7.7, 47.96) * mm, "end": v(7.7, 50.65) * mm});
            skLineSegment(sketch, "E343", {"start": v(7.7, 50.65) * mm, "end": v(7.7, 54.58) * mm});
            skLineSegment(sketch, "E344", {"start": v(7.7, 54.58) * mm, "end": v(4.03, 51.98) * mm});
            skLineSegment(sketch, "E345", {"start": v(4.03, 51.98) * mm, "end": v(1.93, 49.02) * mm});
            skLineSegment(sketch, "E346", {"start": v(1.93, 49.02) * mm, "end": v(3.73, 45.15) * mm});
            skLineSegment(sketch, "E347", {"start": v(-7.65, -35.5) * mm, "end": v(-0.64, -27.93) * mm});
            skLineSegment(sketch, "E348.bottom", {"start": v(-35.04, -65.92) * mm, "end": v(35.04, -65.92) * mm, "construction": true});
            skLineSegment(sketch, "E348.top", {"start": v(-35.04, 65.18) * mm, "end": v(35.04, 65.18) * mm, "construction": true});
            skLineSegment(sketch, "E348.left", {"start": v(-35.04, -65.92) * mm, "end": v(-35.04, 65.18) * mm, "construction": true});
            skLineSegment(sketch, "E348.right", {"start": v(35.04, -65.92) * mm, "end": v(35.04, 65.18) * mm, "construction": true});
            skEllipse(sketch, "E349", {"center": v(0, 0) * mm, "majorRadius": 86.13 * mm, "minorRadius": 42.76 * mm, "majorAxis": v(0, -1)});
            skCircle(sketch, "E350", {"center": v(0, 76.96) * mm, "radius": 6.99 * mm});
            skLineSegment(sketch, "E351", {"start": v(42.76, -0.37) * mm, "end": v(-42.76, -0.37) * mm, "construction": true});
            skPoint(sketch, "E351.startSnap0", {"position": v(35.04, -0.37) * mm});
            skLineSegment(sketch, "E352", {"start": v(0.4, -56.22) * mm, "end": v(5.95, -52.19) * mm});
            skLineSegment(sketch, "E353", {"start": v(-15, 21.64) * mm, "end": v(-11.65, 20.71) * mm});
            skLineSegment(sketch, "E354", {"start": v(-42.76, 0) * mm, "end": v(42.76, 0) * mm, "construction": true});
            skLineSegment(sketch, "E355", {"start": v(0, 86.13) * mm, "end": v(0, 83.94) * mm});
            skSolve(sketch);
        }
        {
            var Q0;
            Q0=makeQuery(id+"F0.imprint","IMPRINT",FACE,{"disambiguationData":[TD([[makeQuery(id+"F0.imprint","IMPRINT",EDGE,{"derivedFrom":sQuery(id+"F0.wireOp",EDGE,"E0")}),-1.0]])]});
            extrude(context, id + "F1", {"entities" : qUnion([Q0]), "depth" : 5.08 * mm, "offsetDistance" : 25.4 * mm});
        }
        {
            var Q0;
            Q0=makeQuery(id+"F1.opExtrude","SWEPT_BODY",BODY,{"disambiguationData":[OSD([sQuery(id+"F0.wireOp",EDGE,"E0"),sQuery(id+"F0.wireOp",EDGE,"E1"),sQuery(id+"F0.wireOp",EDGE,"E2"),sQuery(id+"F0.wireOp",EDGE,"E3"),sQuery(id+"F0.wireOp",EDGE,"E4"),sQuery(id+"F0.wireOp",EDGE,"E5"),sQuery(id+"F0.wireOp",EDGE,"E6"),sQuery(id+"F0.wireOp",EDGE,"E7"),sQuery(id+"F0.wireOp",EDGE,"E8"),sQuery(id+"F0.wireOp",EDGE,"E9"),sQuery(id+"F0.wireOp",EDGE,"E10"),sQuery(id+"F0.wireOp",EDGE,"E11"),sQuery(id+"F0.wireOp",EDGE,"E12"),sQuery(id+"F0.wireOp",EDGE,"E13"),sQuery(id+"F0.wireOp",EDGE,"E14"),sQuery(id+"F0.wireOp",EDGE,"E15"),sQuery(id+"F0.wireOp",EDGE,"E16"),sQuery(id+"F0.wireOp",EDGE,"E17"),sQuery(id+"F0.wireOp",EDGE,"E18"),sQuery(id+"F0.wireOp",EDGE,"E19"),sQuery(id+"F0.wireOp",EDGE,"E20"),sQuery(id+"F0.wireOp",EDGE,"E21"),sQuery(id+"F0.wireOp",EDGE,"E22"),sQuery(id+"F0.wireOp",EDGE,"E23"),sQuery(id+"F0.wireOp",EDGE,"E24"),sQuery(id+"F0.wireOp",EDGE,"E25"),sQuery(id+"F0.wireOp",EDGE,"E26"),sQuery(id+"F0.wireOp",EDGE,"E27"),sQuery(id+"F0.wireOp",EDGE,"E28"),sQuery(id+"F0.wireOp",EDGE,"E29"),sQuery(id+"F0.wireOp",EDGE,"E30"),sQuery(id+"F0.wireOp",EDGE,"E31"),sQuery(id+"F0.wireOp",EDGE,"E32"),sQuery(id+"F0.wireOp",EDGE,"E33"),sQuery(id+"F0.wireOp",EDGE,"E34"),sQuery(id+"F0.wireOp",EDGE,"E35"),sQuery(id+"F0.wireOp",EDGE,"E36"),sQuery(id+"F0.wireOp",EDGE,"E37"),sQuery(id+"F0.wireOp",EDGE,"E38"),sQuery(id+"F0.wireOp",EDGE,"E39"),sQuery(id+"F0.wireOp",EDGE,"E40"),sQuery(id+"F0.wireOp",EDGE,"E41"),sQuery(id+"F0.wireOp",EDGE,"E42"),sQuery(id+"F0.wireOp",EDGE,"E43"),sQuery(id+"F0.wireOp",EDGE,"E44"),sQuery(id+"F0.wireOp",EDGE,"E45"),sQuery(id+"F0.wireOp",EDGE,"E46"),sQuery(id+"F0.wireOp",EDGE,"E47"),sQuery(id+"F0.wireOp",EDGE,"E48"),sQuery(id+"F0.wireOp",EDGE,"E49"),sQuery(id+"F0.wireOp",EDGE,"E50"),sQuery(id+"F0.wireOp",EDGE,"E51"),sQuery(id+"F0.wireOp",EDGE,"E52"),sQuery(id+"F0.wireOp",EDGE,"E53"),sQuery(id+"F0.wireOp",EDGE,"E54"),sQuery(id+"F0.wireOp",EDGE,"E55"),sQuery(id+"F0.wireOp",EDGE,"E56"),sQuery(id+"F0.wireOp",EDGE,"E57"),sQuery(id+"F0.wireOp",EDGE,"E58"),sQuery(id+"F0.wireOp",EDGE,"E59"),sQuery(id+"F0.wireOp",EDGE,"E60"),sQuery(id+"F0.wireOp",EDGE,"E61"),sQuery(id+"F0.wireOp",EDGE,"E62"),sQuery(id+"F0.wireOp",EDGE,"E63"),sQuery(id+"F0.wireOp",EDGE,"E64"),sQuery(id+"F0.wireOp",EDGE,"E65"),sQuery(id+"F0.wireOp",EDGE,"E66"),sQuery(id+"F0.wireOp",EDGE,"E67"),sQuery(id+"F0.wireOp",EDGE,"E68"),sQuery(id+"F0.wireOp",EDGE,"E72"),sQuery(id+"F0.wireOp",EDGE,"E73"),sQuery(id+"F0.wireOp",EDGE,"E74"),sQuery(id+"F0.wireOp",EDGE,"E75"),sQuery(id+"F0.wireOp",EDGE,"E76"),sQuery(id+"F0.wireOp",EDGE,"E77"),sQuery(id+"F0.wireOp",EDGE,"E78"),sQuery(id+"F0.wireOp",EDGE,"E79"),sQuery(id+"F0.wireOp",EDGE,"E80"),sQuery(id+"F0.wireOp",EDGE,"E81"),sQuery(id+"F0.wireOp",EDGE,"E82"),sQuery(id+"F0.wireOp",EDGE,"E83"),sQuery(id+"F0.wireOp",EDGE,"E84"),sQuery(id+"F0.wireOp",EDGE,"E85"),sQuery(id+"F0.wireOp",EDGE,"E86"),sQuery(id+"F0.wireOp",EDGE,"E87"),sQuery(id+"F0.wireOp",EDGE,"E88"),sQuery(id+"F0.wireOp",EDGE,"E89"),sQuery(id+"F0.wireOp",EDGE,"E90"),sQuery(id+"F0.wireOp",EDGE,"E91"),sQuery(id+"F0.wireOp",EDGE,"E92"),sQuery(id+"F0.wireOp",EDGE,"E93"),sQuery(id+"F0.wireOp",EDGE,"E94"),sQuery(id+"F0.wireOp",EDGE,"E95"),sQuery(id+"F0.wireOp",EDGE,"E96"),sQuery(id+"F0.wireOp",EDGE,"E97"),sQuery(id+"F0.wireOp",EDGE,"E98"),sQuery(id+"F0.wireOp",EDGE,"E99"),sQuery(id+"F0.wireOp",EDGE,"E100"),sQuery(id+"F0.wireOp",EDGE,"E101"),sQuery(id+"F0.wireOp",EDGE,"E102"),sQuery(id+"F0.wireOp",EDGE,"E103"),sQuery(id+"F0.wireOp",EDGE,"E104"),sQuery(id+"F0.wireOp",EDGE,"E105"),sQuery(id+"F0.wireOp",EDGE,"E106"),sQuery(id+"F0.wireOp",EDGE,"E107"),sQuery(id+"F0.wireOp",EDGE,"E108"),sQuery(id+"F0.wireOp",EDGE,"E109"),sQuery(id+"F0.wireOp",EDGE,"E110"),sQuery(id+"F0.wireOp",EDGE,"E111"),sQuery(id+"F0.wireOp",EDGE,"E112"),sQuery(id+"F0.wireOp",EDGE,"E113"),sQuery(id+"F0.wireOp",EDGE,"E114"),sQuery(id+"F0.wireOp",EDGE,"E115"),sQuery(id+"F0.wireOp",EDGE,"E116"),sQuery(id+"F0.wireOp",EDGE,"E117"),sQuery(id+"F0.wireOp",EDGE,"E118"),sQuery(id+"F0.wireOp",EDGE,"E119"),sQuery(id+"F0.wireOp",EDGE,"E120"),sQuery(id+"F0.wireOp",EDGE,"E121"),sQuery(id+"F0.wireOp",EDGE,"E122"),sQuery(id+"F0.wireOp",EDGE,"E123"),sQuery(id+"F0.wireOp",EDGE,"E124"),sQuery(id+"F0.wireOp",EDGE,"E125"),sQuery(id+"F0.wireOp",EDGE,"E126"),sQuery(id+"F0.wireOp",EDGE,"E127"),sQuery(id+"F0.wireOp",EDGE,"E128"),sQuery(id+"F0.wireOp",EDGE,"E129"),sQuery(id+"F0.wireOp",EDGE,"E130"),sQuery(id+"F0.wireOp",EDGE,"E131"),sQuery(id+"F0.wireOp",EDGE,"E132"),sQuery(id+"F0.wireOp",EDGE,"E133"),sQuery(id+"F0.wireOp",EDGE,"E134"),sQuery(id+"F0.wireOp",EDGE,"E135"),sQuery(id+"F0.wireOp",EDGE,"E136"),sQuery(id+"F0.wireOp",EDGE,"E137"),sQuery(id+"F0.wireOp",EDGE,"E138"),sQuery(id+"F0.wireOp",EDGE,"E139"),sQuery(id+"F0.wireOp",EDGE,"E140"),sQuery(id+"F0.wireOp",EDGE,"E141"),sQuery(id+"F0.wireOp",EDGE,"E142"),sQuery(id+"F0.wireOp",EDGE,"E143"),sQuery(id+"F0.wireOp",EDGE,"E144"),sQuery(id+"F0.wireOp",EDGE,"E145"),sQuery(id+"F0.wireOp",EDGE,"E146"),sQuery(id+"F0.wireOp",EDGE,"E147"),sQuery(id+"F0.wireOp",EDGE,"E148"),sQuery(id+"F0.wireOp",EDGE,"E149"),sQuery(id+"F0.wireOp",EDGE,"E150"),sQuery(id+"F0.wireOp",EDGE,"E151"),sQuery(id+"F0.wireOp",EDGE,"E152"),sQuery(id+"F0.wireOp",EDGE,"E153"),sQuery(id+"F0.wireOp",EDGE,"E154"),sQuery(id+"F0.wireOp",EDGE,"E155"),sQuery(id+"F0.wireOp",EDGE,"E156"),sQuery(id+"F0.wireOp",EDGE,"E157"),sQuery(id+"F0.wireOp",EDGE,"E158"),sQuery(id+"F0.wireOp",EDGE,"E159"),sQuery(id+"F0.wireOp",EDGE,"E160"),sQuery(id+"F0.wireOp",EDGE,"E161"),sQuery(id+"F0.wireOp",EDGE,"E162"),sQuery(id+"F0.wireOp",EDGE,"E163"),sQuery(id+"F0.wireOp",EDGE,"E164"),sQuery(id+"F0.wireOp",EDGE,"E165"),sQuery(id+"F0.wireOp",EDGE,"E166"),sQuery(id+"F0.wireOp",EDGE,"E167"),sQuery(id+"F0.wireOp",EDGE,"E168"),sQuery(id+"F0.wireOp",EDGE,"E169"),sQuery(id+"F0.wireOp",EDGE,"E170"),sQuery(id+"F0.wireOp",EDGE,"E171"),sQuery(id+"F0.wireOp",EDGE,"E172"),sQuery(id+"F0.wireOp",EDGE,"E173"),sQuery(id+"F0.wireOp",EDGE,"E174"),sQuery(id+"F0.wireOp",EDGE,"E175"),sQuery(id+"F0.wireOp",EDGE,"E176"),sQuery(id+"F0.wireOp",EDGE,"E177"),sQuery(id+"F0.wireOp",EDGE,"E178"),sQuery(id+"F0.wireOp",EDGE,"E179"),sQuery(id+"F0.wireOp",EDGE,"E180"),sQuery(id+"F0.wireOp",EDGE,"E181"),sQuery(id+"F0.wireOp",EDGE,"E182"),sQuery(id+"F0.wireOp",EDGE,"E183"),sQuery(id+"F0.wireOp",EDGE,"E184"),sQuery(id+"F0.wireOp",EDGE,"E185"),sQuery(id+"F0.wireOp",EDGE,"E186"),sQuery(id+"F0.wireOp",EDGE,"E187"),sQuery(id+"F0.wireOp",EDGE,"E188"),sQuery(id+"F0.wireOp",EDGE,"E189"),sQuery(id+"F0.wireOp",EDGE,"E190"),sQuery(id+"F0.wireOp",EDGE,"E191"),sQuery(id+"F0.wireOp",EDGE,"E192"),sQuery(id+"F0.wireOp",EDGE,"E193"),sQuery(id+"F0.wireOp",EDGE,"E194"),sQuery(id+"F0.wireOp",EDGE,"E195"),sQuery(id+"F0.wireOp",EDGE,"E196"),sQuery(id+"F0.wireOp",EDGE,"E197"),sQuery(id+"F0.wireOp",EDGE,"E198"),sQuery(id+"F0.wireOp",EDGE,"E199"),sQuery(id+"F0.wireOp",EDGE,"E200"),sQuery(id+"F0.wireOp",EDGE,"E201"),sQuery(id+"F0.wireOp",EDGE,"E202"),sQuery(id+"F0.wireOp",EDGE,"E203"),sQuery(id+"F0.wireOp",EDGE,"E204"),sQuery(id+"F0.wireOp",EDGE,"E205"),sQuery(id+"F0.wireOp",EDGE,"E206"),sQuery(id+"F0.wireOp",EDGE,"E207"),sQuery(id+"F0.wireOp",EDGE,"E208"),sQuery(id+"F0.wireOp",EDGE,"E209"),sQuery(id+"F0.wireOp",EDGE,"E210"),sQuery(id+"F0.wireOp",EDGE,"E211"),sQuery(id+"F0.wireOp",EDGE,"E212"),sQuery(id+"F0.wireOp",EDGE,"E213"),sQuery(id+"F0.wireOp",EDGE,"E214"),sQuery(id+"F0.wireOp",EDGE,"E215"),sQuery(id+"F0.wireOp",EDGE,"E216"),sQuery(id+"F0.wireOp",EDGE,"E217"),sQuery(id+"F0.wireOp",EDGE,"E218"),sQuery(id+"F0.wireOp",EDGE,"E219"),sQuery(id+"F0.wireOp",EDGE,"E220"),sQuery(id+"F0.wireOp",EDGE,"E221"),sQuery(id+"F0.wireOp",EDGE,"E222"),sQuery(id+"F0.wireOp",EDGE,"E223"),sQuery(id+"F0.wireOp",EDGE,"E224"),sQuery(id+"F0.wireOp",EDGE,"E225"),sQuery(id+"F0.wireOp",EDGE,"E226"),sQuery(id+"F0.wireOp",EDGE,"E227"),sQuery(id+"F0.wireOp",EDGE,"E228"),sQuery(id+"F0.wireOp",EDGE,"E229"),sQuery(id+"F0.wireOp",EDGE,"E230"),sQuery(id+"F0.wireOp",EDGE,"E231"),sQuery(id+"F0.wireOp",EDGE,"E232"),sQuery(id+"F0.wireOp",EDGE,"E233"),sQuery(id+"F0.wireOp",EDGE,"E234"),sQuery(id+"F0.wireOp",EDGE,"E235"),sQuery(id+"F0.wireOp",EDGE,"E236"),sQuery(id+"F0.wireOp",EDGE,"E237"),sQuery(id+"F0.wireOp",EDGE,"E238"),sQuery(id+"F0.wireOp",EDGE,"E239"),sQuery(id+"F0.wireOp",EDGE,"E240"),sQuery(id+"F0.wireOp",EDGE,"335e49da-e290-4d69-b9ee-bf74629cb29d"),sQuery(id+"F0.wireOp",EDGE,"a13d8cb5-f6a6-43dd-bdbe-38a068e7ae1e"),sQuery(id+"F0.wireOp",EDGE,"E241"),sQuery(id+"F0.wireOp",EDGE,"E242"),sQuery(id+"F0.wireOp",EDGE,"E243"),sQuery(id+"F0.wireOp",EDGE,"E244"),sQuery(id+"F0.wireOp",EDGE,"E245"),sQuery(id+"F0.wireOp",EDGE,"E246"),sQuery(id+"F0.wireOp",EDGE,"E247"),sQuery(id+"F0.wireOp",EDGE,"E248"),sQuery(id+"F0.wireOp",EDGE,"E249"),sQuery(id+"F0.wireOp",EDGE,"E250"),sQuery(id+"F0.wireOp",EDGE,"E251"),sQuery(id+"F0.wireOp",EDGE,"E252"),sQuery(id+"F0.wireOp",EDGE,"E253"),sQuery(id+"F0.wireOp",EDGE,"E254"),sQuery(id+"F0.wireOp",EDGE,"E255"),sQuery(id+"F0.wireOp",EDGE,"E256"),sQuery(id+"F0.wireOp",EDGE,"E257"),sQuery(id+"F0.wireOp",EDGE,"E258"),sQuery(id+"F0.wireOp",EDGE,"E259"),sQuery(id+"F0.wireOp",EDGE,"E260"),sQuery(id+"F0.wireOp",EDGE,"E261"),sQuery(id+"F0.wireOp",EDGE,"E262"),sQuery(id+"F0.wireOp",EDGE,"E263"),sQuery(id+"F0.wireOp",EDGE,"E264"),sQuery(id+"F0.wireOp",EDGE,"E265"),sQuery(id+"F0.wireOp",EDGE,"E266"),sQuery(id+"F0.wireOp",EDGE,"E267"),sQuery(id+"F0.wireOp",EDGE,"E268"),sQuery(id+"F0.wireOp",EDGE,"E269"),sQuery(id+"F0.wireOp",EDGE,"E270"),sQuery(id+"F0.wireOp",EDGE,"E271"),sQuery(id+"F0.wireOp",EDGE,"E272"),sQuery(id+"F0.wireOp",EDGE,"E273"),sQuery(id+"F0.wireOp",EDGE,"E274"),sQuery(id+"F0.wireOp",EDGE,"E275"),sQuery(id+"F0.wireOp",EDGE,"E276"),sQuery(id+"F0.wireOp",EDGE,"E277"),sQuery(id+"F0.wireOp",EDGE,"E278"),sQuery(id+"F0.wireOp",EDGE,"E279"),sQuery(id+"F0.wireOp",EDGE,"E280"),sQuery(id+"F0.wireOp",EDGE,"E281"),sQuery(id+"F0.wireOp",EDGE,"E282"),sQuery(id+"F0.wireOp",EDGE,"E283"),sQuery(id+"F0.wireOp",EDGE,"E284"),sQuery(id+"F0.wireOp",EDGE,"E285"),sQuery(id+"F0.wireOp",EDGE,"E286"),sQuery(id+"F0.wireOp",EDGE,"E287"),sQuery(id+"F0.wireOp",EDGE,"E288"),sQuery(id+"F0.wireOp",EDGE,"E289"),sQuery(id+"F0.wireOp",EDGE,"E290"),sQuery(id+"F0.wireOp",EDGE,"E291"),sQuery(id+"F0.wireOp",EDGE,"E292"),sQuery(id+"F0.wireOp",EDGE,"E293"),sQuery(id+"F0.wireOp",EDGE,"E294"),sQuery(id+"F0.wireOp",EDGE,"E295"),sQuery(id+"F0.wireOp",EDGE,"E296"),sQuery(id+"F0.wireOp",EDGE,"E297"),sQuery(id+"F0.wireOp",EDGE,"E298"),sQuery(id+"F0.wireOp",EDGE,"E299"),sQuery(id+"F0.wireOp",EDGE,"E300"),sQuery(id+"F0.wireOp",EDGE,"E301"),sQuery(id+"F0.wireOp",EDGE,"E302"),sQuery(id+"F0.wireOp",EDGE,"E303"),sQuery(id+"F0.wireOp",EDGE,"E304"),sQuery(id+"F0.wireOp",EDGE,"E305"),sQuery(id+"F0.wireOp",EDGE,"E306"),sQuery(id+"F0.wireOp",EDGE,"E307"),sQuery(id+"F0.wireOp",EDGE,"E308"),sQuery(id+"F0.wireOp",EDGE,"E309"),sQuery(id+"F0.wireOp",EDGE,"E310"),sQuery(id+"F0.wireOp",EDGE,"E311"),sQuery(id+"F0.wireOp",EDGE,"E312"),sQuery(id+"F0.wireOp",EDGE,"E313"),sQuery(id+"F0.wireOp",EDGE,"E314"),sQuery(id+"F0.wireOp",EDGE,"E315"),sQuery(id+"F0.wireOp",EDGE,"E316"),sQuery(id+"F0.wireOp",EDGE,"E317"),sQuery(id+"F0.wireOp",EDGE,"E318"),sQuery(id+"F0.wireOp",EDGE,"E319"),sQuery(id+"F0.wireOp",EDGE,"E320"),sQuery(id+"F0.wireOp",EDGE,"E321"),sQuery(id+"F0.wireOp",EDGE,"E322"),sQuery(id+"F0.wireOp",EDGE,"E323"),sQuery(id+"F0.wireOp",EDGE,"E324"),sQuery(id+"F0.wireOp",EDGE,"E325"),sQuery(id+"F0.wireOp",EDGE,"E326"),sQuery(id+"F0.wireOp",EDGE,"E327"),sQuery(id+"F0.wireOp",EDGE,"E328"),sQuery(id+"F0.wireOp",EDGE,"E329"),sQuery(id+"F0.wireOp",EDGE,"E330"),sQuery(id+"F0.wireOp",EDGE,"E331"),sQuery(id+"F0.wireOp",EDGE,"E332"),sQuery(id+"F0.wireOp",EDGE,"E333"),sQuery(id+"F0.wireOp",EDGE,"E334"),sQuery(id+"F0.wireOp",EDGE,"E335"),sQuery(id+"F0.wireOp",EDGE,"E336"),sQuery(id+"F0.wireOp",EDGE,"E337"),sQuery(id+"F0.wireOp",EDGE,"E338"),sQuery(id+"F0.wireOp",EDGE,"E339"),sQuery(id+"F0.wireOp",EDGE,"E340"),sQuery(id+"F0.wireOp",EDGE,"E341"),sQuery(id+"F0.wireOp",EDGE,"E342"),sQuery(id+"F0.wireOp",EDGE,"E343"),sQuery(id+"F0.wireOp",EDGE,"E344"),sQuery(id+"F0.wireOp",EDGE,"E345"),sQuery(id+"F0.wireOp",EDGE,"E346"),sQuery(id+"F0.wireOp",EDGE,"E347"),sQuery(id+"F0.wireOp",EDGE,"E349"),sQuery(id+"F0.wireOp",EDGE,"E350")])]});
            var Q1;
            Q1=sQuery(id+"F0.wireOp",VERTEX,"E349.center");
            transform(context, id + "F2", {"entities" : qUnion([Q0]), "transformType" : TransformType.SCALE_UNIFORMLY, "scale" : 0.6, "scalePoint" : qUnion([Q1]), "makeCopy" : false});
        }
        {
            var Q0;
            Q0=makeQuery(id+"F1.opExtrude","CAP_FACE",FACE,{"disambiguationData":[OSD([sQuery(id+"F0.wireOp",EDGE,"E0"),sQuery(id+"F0.wireOp",EDGE,"E1"),sQuery(id+"F0.wireOp",EDGE,"E2"),sQuery(id+"F0.wireOp",EDGE,"E3"),sQuery(id+"F0.wireOp",EDGE,"E4"),sQuery(id+"F0.wireOp",EDGE,"E5"),sQuery(id+"F0.wireOp",EDGE,"E6"),sQuery(id+"F0.wireOp",EDGE,"E7"),sQuery(id+"F0.wireOp",EDGE,"E8"),sQuery(id+"F0.wireOp",EDGE,"E9"),sQuery(id+"F0.wireOp",EDGE,"E10"),sQuery(id+"F0.wireOp",EDGE,"E11"),sQuery(id+"F0.wireOp",EDGE,"E12"),sQuery(id+"F0.wireOp",EDGE,"E13"),sQuery(id+"F0.wireOp",EDGE,"E14"),sQuery(id+"F0.wireOp",EDGE,"E15"),sQuery(id+"F0.wireOp",EDGE,"E16"),sQuery(id+"F0.wireOp",EDGE,"E17"),sQuery(id+"F0.wireOp",EDGE,"E18"),sQuery(id+"F0.wireOp",EDGE,"E19"),sQuery(id+"F0.wireOp",EDGE,"E20"),sQuery(id+"F0.wireOp",EDGE,"E21"),sQuery(id+"F0.wireOp",EDGE,"E22"),sQuery(id+"F0.wireOp",EDGE,"E23"),sQuery(id+"F0.wireOp",EDGE,"E24"),sQuery(id+"F0.wireOp",EDGE,"E25"),sQuery(id+"F0.wireOp",EDGE,"E26"),sQuery(id+"F0.wireOp",EDGE,"E27"),sQuery(id+"F0.wireOp",EDGE,"E28"),sQuery(id+"F0.wireOp",EDGE,"E29"),sQuery(id+"F0.wireOp",EDGE,"E30"),sQuery(id+"F0.wireOp",EDGE,"E31"),sQuery(id+"F0.wireOp",EDGE,"E32"),sQuery(id+"F0.wireOp",EDGE,"E33"),sQuery(id+"F0.wireOp",EDGE,"E34"),sQuery(id+"F0.wireOp",EDGE,"E35"),sQuery(id+"F0.wireOp",EDGE,"E36"),sQuery(id+"F0.wireOp",EDGE,"E37"),sQuery(id+"F0.wireOp",EDGE,"E38"),sQuery(id+"F0.wireOp",EDGE,"E39"),sQuery(id+"F0.wireOp",EDGE,"E40"),sQuery(id+"F0.wireOp",EDGE,"E41"),sQuery(id+"F0.wireOp",EDGE,"E42"),sQuery(id+"F0.wireOp",EDGE,"E43"),sQuery(id+"F0.wireOp",EDGE,"E44"),sQuery(id+"F0.wireOp",EDGE,"E45"),sQuery(id+"F0.wireOp",EDGE,"E46"),sQuery(id+"F0.wireOp",EDGE,"E47"),sQuery(id+"F0.wireOp",EDGE,"E48"),sQuery(id+"F0.wireOp",EDGE,"E49"),sQuery(id+"F0.wireOp",EDGE,"E50"),sQuery(id+"F0.wireOp",EDGE,"E51"),sQuery(id+"F0.wireOp",EDGE,"E52"),sQuery(id+"F0.wireOp",EDGE,"E53"),sQuery(id+"F0.wireOp",EDGE,"E54"),sQuery(id+"F0.wireOp",EDGE,"E55"),sQuery(id+"F0.wireOp",EDGE,"E56"),sQuery(id+"F0.wireOp",EDGE,"E57"),sQuery(id+"F0.wireOp",EDGE,"E58"),sQuery(id+"F0.wireOp",EDGE,"E59"),sQuery(id+"F0.wireOp",EDGE,"E60"),sQuery(id+"F0.wireOp",EDGE,"E61"),sQuery(id+"F0.wireOp",EDGE,"E62"),sQuery(id+"F0.wireOp",EDGE,"E63"),sQuery(id+"F0.wireOp",EDGE,"E64"),sQuery(id+"F0.wireOp",EDGE,"E65"),sQuery(id+"F0.wireOp",EDGE,"E66"),sQuery(id+"F0.wireOp",EDGE,"E67"),sQuery(id+"F0.wireOp",EDGE,"E68"),sQuery(id+"F0.wireOp",EDGE,"E69"),sQuery(id+"F0.wireOp",EDGE,"E70"),sQuery(id+"F0.wireOp",EDGE,"E71"),sQuery(id+"F0.wireOp",EDGE,"E72"),sQuery(id+"F0.wireOp",EDGE,"E73"),sQuery(id+"F0.wireOp",EDGE,"E74"),sQuery(id+"F0.wireOp",EDGE,"E75"),sQuery(id+"F0.wireOp",EDGE,"E76"),sQuery(id+"F0.wireOp",EDGE,"E77"),sQuery(id+"F0.wireOp",EDGE,"E78"),sQuery(id+"F0.wireOp",EDGE,"E79"),sQuery(id+"F0.wireOp",EDGE,"E80"),sQuery(id+"F0.wireOp",EDGE,"E81"),sQuery(id+"F0.wireOp",EDGE,"E82"),sQuery(id+"F0.wireOp",EDGE,"E83"),sQuery(id+"F0.wireOp",EDGE,"E84"),sQuery(id+"F0.wireOp",EDGE,"E85"),sQuery(id+"F0.wireOp",EDGE,"E86"),sQuery(id+"F0.wireOp",EDGE,"E87"),sQuery(id+"F0.wireOp",EDGE,"E88"),sQuery(id+"F0.wireOp",EDGE,"E89"),sQuery(id+"F0.wireOp",EDGE,"E90"),sQuery(id+"F0.wireOp",EDGE,"E91"),sQuery(id+"F0.wireOp",EDGE,"E92"),sQuery(id+"F0.wireOp",EDGE,"E93"),sQuery(id+"F0.wireOp",EDGE,"E94"),sQuery(id+"F0.wireOp",EDGE,"E95"),sQuery(id+"F0.wireOp",EDGE,"E96"),sQuery(id+"F0.wireOp",EDGE,"E97"),sQuery(id+"F0.wireOp",EDGE,"E98"),sQuery(id+"F0.wireOp",EDGE,"E99"),sQuery(id+"F0.wireOp",EDGE,"E100"),sQuery(id+"F0.wireOp",EDGE,"E101"),sQuery(id+"F0.wireOp",EDGE,"E102"),sQuery(id+"F0.wireOp",EDGE,"E103"),sQuery(id+"F0.wireOp",EDGE,"E104"),sQuery(id+"F0.wireOp",EDGE,"E105"),sQuery(id+"F0.wireOp",EDGE,"E106"),sQuery(id+"F0.wireOp",EDGE,"E107"),sQuery(id+"F0.wireOp",EDGE,"E108"),sQuery(id+"F0.wireOp",EDGE,"E109"),sQuery(id+"F0.wireOp",EDGE,"E110"),sQuery(id+"F0.wireOp",EDGE,"E111"),sQuery(id+"F0.wireOp",EDGE,"E112"),sQuery(id+"F0.wireOp",EDGE,"E113"),sQuery(id+"F0.wireOp",EDGE,"E114"),sQuery(id+"F0.wireOp",EDGE,"E115"),sQuery(id+"F0.wireOp",EDGE,"E116"),sQuery(id+"F0.wireOp",EDGE,"E117"),sQuery(id+"F0.wireOp",EDGE,"E118"),sQuery(id+"F0.wireOp",EDGE,"E119"),sQuery(id+"F0.wireOp",EDGE,"E120"),sQuery(id+"F0.wireOp",EDGE,"E121"),sQuery(id+"F0.wireOp",EDGE,"E122"),sQuery(id+"F0.wireOp",EDGE,"E123"),sQuery(id+"F0.wireOp",EDGE,"E124"),sQuery(id+"F0.wireOp",EDGE,"E125"),sQuery(id+"F0.wireOp",EDGE,"E126"),sQuery(id+"F0.wireOp",EDGE,"E127"),sQuery(id+"F0.wireOp",EDGE,"E128"),sQuery(id+"F0.wireOp",EDGE,"E129"),sQuery(id+"F0.wireOp",EDGE,"E130"),sQuery(id+"F0.wireOp",EDGE,"E131"),sQuery(id+"F0.wireOp",EDGE,"E132"),sQuery(id+"F0.wireOp",EDGE,"E133"),sQuery(id+"F0.wireOp",EDGE,"E134"),sQuery(id+"F0.wireOp",EDGE,"E135"),sQuery(id+"F0.wireOp",EDGE,"E136"),sQuery(id+"F0.wireOp",EDGE,"E137"),sQuery(id+"F0.wireOp",EDGE,"E138"),sQuery(id+"F0.wireOp",EDGE,"E139"),sQuery(id+"F0.wireOp",EDGE,"E140"),sQuery(id+"F0.wireOp",EDGE,"E141"),sQuery(id+"F0.wireOp",EDGE,"E142"),sQuery(id+"F0.wireOp",EDGE,"E143"),sQuery(id+"F0.wireOp",EDGE,"E144"),sQuery(id+"F0.wireOp",EDGE,"E145"),sQuery(id+"F0.wireOp",EDGE,"E146"),sQuery(id+"F0.wireOp",EDGE,"E147"),sQuery(id+"F0.wireOp",EDGE,"E148"),sQuery(id+"F0.wireOp",EDGE,"E149"),sQuery(id+"F0.wireOp",EDGE,"E150"),sQuery(id+"F0.wireOp",EDGE,"E151"),sQuery(id+"F0.wireOp",EDGE,"E152"),sQuery(id+"F0.wireOp",EDGE,"E153"),sQuery(id+"F0.wireOp",EDGE,"E154"),sQuery(id+"F0.wireOp",EDGE,"E155"),sQuery(id+"F0.wireOp",EDGE,"E156"),sQuery(id+"F0.wireOp",EDGE,"E157"),sQuery(id+"F0.wireOp",EDGE,"E158"),sQuery(id+"F0.wireOp",EDGE,"E159"),sQuery(id+"F0.wireOp",EDGE,"E160"),sQuery(id+"F0.wireOp",EDGE,"E161"),sQuery(id+"F0.wireOp",EDGE,"E162"),sQuery(id+"F0.wireOp",EDGE,"E163"),sQuery(id+"F0.wireOp",EDGE,"E164"),sQuery(id+"F0.wireOp",EDGE,"E165"),sQuery(id+"F0.wireOp",EDGE,"E166"),sQuery(id+"F0.wireOp",EDGE,"E167"),sQuery(id+"F0.wireOp",EDGE,"E168"),sQuery(id+"F0.wireOp",EDGE,"E169"),sQuery(id+"F0.wireOp",EDGE,"E170"),sQuery(id+"F0.wireOp",EDGE,"E171"),sQuery(id+"F0.wireOp",EDGE,"E172"),sQuery(id+"F0.wireOp",EDGE,"E173"),sQuery(id+"F0.wireOp",EDGE,"E174"),sQuery(id+"F0.wireOp",EDGE,"E175"),sQuery(id+"F0.wireOp",EDGE,"E176"),sQuery(id+"F0.wireOp",EDGE,"E177"),sQuery(id+"F0.wireOp",EDGE,"E178"),sQuery(id+"F0.wireOp",EDGE,"E179"),sQuery(id+"F0.wireOp",EDGE,"E180"),sQuery(id+"F0.wireOp",EDGE,"E181"),sQuery(id+"F0.wireOp",EDGE,"E182"),sQuery(id+"F0.wireOp",EDGE,"E183"),sQuery(id+"F0.wireOp",EDGE,"E184"),sQuery(id+"F0.wireOp",EDGE,"E185"),sQuery(id+"F0.wireOp",EDGE,"E186"),sQuery(id+"F0.wireOp",EDGE,"E187"),sQuery(id+"F0.wireOp",EDGE,"E188"),sQuery(id+"F0.wireOp",EDGE,"E189"),sQuery(id+"F0.wireOp",EDGE,"E190"),sQuery(id+"F0.wireOp",EDGE,"E191"),sQuery(id+"F0.wireOp",EDGE,"E192"),sQuery(id+"F0.wireOp",EDGE,"E193"),sQuery(id+"F0.wireOp",EDGE,"E194"),sQuery(id+"F0.wireOp",EDGE,"E195"),sQuery(id+"F0.wireOp",EDGE,"E196"),sQuery(id+"F0.wireOp",EDGE,"E197"),sQuery(id+"F0.wireOp",EDGE,"E198"),sQuery(id+"F0.wireOp",EDGE,"E199"),sQuery(id+"F0.wireOp",EDGE,"E200"),sQuery(id+"F0.wireOp",EDGE,"E201"),sQuery(id+"F0.wireOp",EDGE,"E202"),sQuery(id+"F0.wireOp",EDGE,"E203"),sQuery(id+"F0.wireOp",EDGE,"E204"),sQuery(id+"F0.wireOp",EDGE,"E205"),sQuery(id+"F0.wireOp",EDGE,"E206"),sQuery(id+"F0.wireOp",EDGE,"E207"),sQuery(id+"F0.wireOp",EDGE,"E208"),sQuery(id+"F0.wireOp",EDGE,"E209"),sQuery(id+"F0.wireOp",EDGE,"E210"),sQuery(id+"F0.wireOp",EDGE,"E211"),sQuery(id+"F0.wireOp",EDGE,"E212"),sQuery(id+"F0.wireOp",EDGE,"E213"),sQuery(id+"F0.wireOp",EDGE,"E214"),sQuery(id+"F0.wireOp",EDGE,"E215"),sQuery(id+"F0.wireOp",EDGE,"E216"),sQuery(id+"F0.wireOp",EDGE,"E217"),sQuery(id+"F0.wireOp",EDGE,"E218"),sQuery(id+"F0.wireOp",EDGE,"E219"),sQuery(id+"F0.wireOp",EDGE,"E220"),sQuery(id+"F0.wireOp",EDGE,"E221"),sQuery(id+"F0.wireOp",EDGE,"E222"),sQuery(id+"F0.wireOp",EDGE,"E223"),sQuery(id+"F0.wireOp",EDGE,"E224"),sQuery(id+"F0.wireOp",EDGE,"E225"),sQuery(id+"F0.wireOp",EDGE,"E226"),sQuery(id+"F0.wireOp",EDGE,"E227"),sQuery(id+"F0.wireOp",EDGE,"E228"),sQuery(id+"F0.wireOp",EDGE,"E229"),sQuery(id+"F0.wireOp",EDGE,"E230"),sQuery(id+"F0.wireOp",EDGE,"E231"),sQuery(id+"F0.wireOp",EDGE,"E232"),sQuery(id+"F0.wireOp",EDGE,"E233"),sQuery(id+"F0.wireOp",EDGE,"E234"),sQuery(id+"F0.wireOp",EDGE,"E235"),sQuery(id+"F0.wireOp",EDGE,"E236"),sQuery(id+"F0.wireOp",EDGE,"E237"),sQuery(id+"F0.wireOp",EDGE,"E238"),sQuery(id+"F0.wireOp",EDGE,"E239"),sQuery(id+"F0.wireOp",EDGE,"E240"),sQuery(id+"F0.wireOp",EDGE,"E241"),sQuery(id+"F0.wireOp",EDGE,"E242"),sQuery(id+"F0.wireOp",EDGE,"E243"),sQuery(id+"F0.wireOp",EDGE,"E244"),sQuery(id+"F0.wireOp",EDGE,"E245"),sQuery(id+"F0.wireOp",EDGE,"E246"),sQuery(id+"F0.wireOp",EDGE,"E247"),sQuery(id+"F0.wireOp",EDGE,"E248"),sQuery(id+"F0.wireOp",EDGE,"E249"),sQuery(id+"F0.wireOp",EDGE,"E250"),sQuery(id+"F0.wireOp",EDGE,"E251"),sQuery(id+"F0.wireOp",EDGE,"E252"),sQuery(id+"F0.wireOp",EDGE,"E253"),sQuery(id+"F0.wireOp",EDGE,"E254"),sQuery(id+"F0.wireOp",EDGE,"E255"),sQuery(id+"F0.wireOp",EDGE,"E256"),sQuery(id+"F0.wireOp",EDGE,"E257"),sQuery(id+"F0.wireOp",EDGE,"E258"),sQuery(id+"F0.wireOp",EDGE,"E259"),sQuery(id+"F0.wireOp",EDGE,"E260"),sQuery(id+"F0.wireOp",EDGE,"E261"),sQuery(id+"F0.wireOp",EDGE,"E262"),sQuery(id+"F0.wireOp",EDGE,"E263"),sQuery(id+"F0.wireOp",EDGE,"E264"),sQuery(id+"F0.wireOp",EDGE,"E265"),sQuery(id+"F0.wireOp",EDGE,"E266"),sQuery(id+"F0.wireOp",EDGE,"E267"),sQuery(id+"F0.wireOp",EDGE,"E268"),sQuery(id+"F0.wireOp",EDGE,"E269"),sQuery(id+"F0.wireOp",EDGE,"E270"),sQuery(id+"F0.wireOp",EDGE,"E271"),sQuery(id+"F0.wireOp",EDGE,"E272"),sQuery(id+"F0.wireOp",EDGE,"E273"),sQuery(id+"F0.wireOp",EDGE,"E274"),sQuery(id+"F0.wireOp",EDGE,"E275"),sQuery(id+"F0.wireOp",EDGE,"E276"),sQuery(id+"F0.wireOp",EDGE,"E277"),sQuery(id+"F0.wireOp",EDGE,"E278"),sQuery(id+"F0.wireOp",EDGE,"E279"),sQuery(id+"F0.wireOp",EDGE,"E280"),sQuery(id+"F0.wireOp",EDGE,"E281"),sQuery(id+"F0.wireOp",EDGE,"E282"),sQuery(id+"F0.wireOp",EDGE,"E283"),sQuery(id+"F0.wireOp",EDGE,"E284"),sQuery(id+"F0.wireOp",EDGE,"E285"),sQuery(id+"F0.wireOp",EDGE,"E286"),sQuery(id+"F0.wireOp",EDGE,"E287"),sQuery(id+"F0.wireOp",EDGE,"E288"),sQuery(id+"F0.wireOp",EDGE,"E289"),sQuery(id+"F0.wireOp",EDGE,"E290"),sQuery(id+"F0.wireOp",EDGE,"E291"),sQuery(id+"F0.wireOp",EDGE,"E292"),sQuery(id+"F0.wireOp",EDGE,"E293"),sQuery(id+"F0.wireOp",EDGE,"E294"),sQuery(id+"F0.wireOp",EDGE,"E295"),sQuery(id+"F0.wireOp",EDGE,"E296"),sQuery(id+"F0.wireOp",EDGE,"E297"),sQuery(id+"F0.wireOp",EDGE,"E298"),sQuery(id+"F0.wireOp",EDGE,"E299"),sQuery(id+"F0.wireOp",EDGE,"E300"),sQuery(id+"F0.wireOp",EDGE,"E301"),sQuery(id+"F0.wireOp",EDGE,"E302"),sQuery(id+"F0.wireOp",EDGE,"E303"),sQuery(id+"F0.wireOp",EDGE,"E304"),sQuery(id+"F0.wireOp",EDGE,"E305"),sQuery(id+"F0.wireOp",EDGE,"E306"),sQuery(id+"F0.wireOp",EDGE,"E307"),sQuery(id+"F0.wireOp",EDGE,"E308"),sQuery(id+"F0.wireOp",EDGE,"E309"),sQuery(id+"F0.wireOp",EDGE,"E310"),sQuery(id+"F0.wireOp",EDGE,"E311"),sQuery(id+"F0.wireOp",EDGE,"E312"),sQuery(id+"F0.wireOp",EDGE,"E313"),sQuery(id+"F0.wireOp",EDGE,"E314"),sQuery(id+"F0.wireOp",EDGE,"E315"),sQuery(id+"F0.wireOp",EDGE,"E316"),sQuery(id+"F0.wireOp",EDGE,"E317"),sQuery(id+"F0.wireOp",EDGE,"E318"),sQuery(id+"F0.wireOp",EDGE,"E319"),sQuery(id+"F0.wireOp",EDGE,"E320"),sQuery(id+"F0.wireOp",EDGE,"E321"),sQuery(id+"F0.wireOp",EDGE,"E322"),sQuery(id+"F0.wireOp",EDGE,"E323"),sQuery(id+"F0.wireOp",EDGE,"E324"),sQuery(id+"F0.wireOp",EDGE,"E325"),sQuery(id+"F0.wireOp",EDGE,"E326"),sQuery(id+"F0.wireOp",EDGE,"E327"),sQuery(id+"F0.wireOp",EDGE,"E328"),sQuery(id+"F0.wireOp",EDGE,"E329"),sQuery(id+"F0.wireOp",EDGE,"E330"),sQuery(id+"F0.wireOp",EDGE,"E331"),sQuery(id+"F0.wireOp",EDGE,"E332"),sQuery(id+"F0.wireOp",EDGE,"E333"),sQuery(id+"F0.wireOp",EDGE,"E334"),sQuery(id+"F0.wireOp",EDGE,"E335"),sQuery(id+"F0.wireOp",EDGE,"E336"),sQuery(id+"F0.wireOp",EDGE,"E337"),sQuery(id+"F0.wireOp",EDGE,"E338"),sQuery(id+"F0.wireOp",EDGE,"E339"),sQuery(id+"F0.wireOp",EDGE,"E340"),sQuery(id+"F0.wireOp",EDGE,"E341"),sQuery(id+"F0.wireOp",EDGE,"E342"),sQuery(id+"F0.wireOp",EDGE,"E343"),sQuery(id+"F0.wireOp",EDGE,"E344"),sQuery(id+"F0.wireOp",EDGE,"E345"),sQuery(id+"F0.wireOp",EDGE,"E346"),sQuery(id+"F0.wireOp",EDGE,"E347"),sQuery(id+"F0.wireOp",EDGE,"E349"),sQuery(id+"F0.wireOp",EDGE,"E350"),sQuery(id+"F0.wireOp",EDGE,"E352"),sQuery(id+"F0.wireOp",EDGE,"E353")])],"isStart":false});
            var sketch = newSketch(context, id + "F3", { "sketchPlane" : qUnion([Q0])});
            skSolve(sketch);
        }
        {
            var Q0;
            Q0=makeQuery(id+"F3.imprint","IMPRINT",FACE,{"disambiguationData":[TD([[makeQuery(id+"F3.imprint","IMPRINT",EDGE,{"derivedFrom":makeQuery(id+"F1.opExtrude","CAP_EDGE",EDGE,{"disambiguationData":[OSD([sQuery(id+"F0.wireOp",EDGE,"E187")])],"isStart":false})}),1.0]])]});
            var Q1;
            Q1=makeQuery(id+"F3.imprint","IMPRINT",FACE,{"disambiguationData":[TD([[makeQuery(id+"F3.imprint","IMPRINT",EDGE,{"derivedFrom":makeQuery(id+"F1.opExtrude","CAP_EDGE",EDGE,{"disambiguationData":[OSD([sQuery(id+"F0.wireOp",EDGE,"E231")])],"isStart":false})}),1.0]])]});
            var Q2;
            Q2=makeQuery(id+"F3.imprint","IMPRINT",FACE,{"disambiguationData":[TD([[makeQuery(id+"F3.imprint","IMPRINT",EDGE,{"derivedFrom":makeQuery(id+"F1.opExtrude","CAP_EDGE",EDGE,{"disambiguationData":[OSD([sQuery(id+"F0.wireOp",EDGE,"E252")])],"isStart":false})}),1.0]])]});
            var Q3;
            Q3=makeQuery(id+"F3.imprint","IMPRINT",FACE,{"disambiguationData":[TD([[makeQuery(id+"F3.imprint","IMPRINT",EDGE,{"derivedFrom":makeQuery(id+"F1.opExtrude","CAP_EDGE",EDGE,{"disambiguationData":[OSD([sQuery(id+"F0.wireOp",EDGE,"E212")])],"isStart":false})}),1.0]])]});
            var Q4;
            Q4=makeQuery(id+"F3.imprint","IMPRINT",FACE,{"disambiguationData":[TD([[makeQuery(id+"F3.imprint","IMPRINT",EDGE,{"derivedFrom":makeQuery(id+"F1.opExtrude","CAP_EDGE",EDGE,{"disambiguationData":[OSD([sQuery(id+"F0.wireOp",EDGE,"E314")])],"isStart":false})}),-1.0]])]});
            var Q5;
            Q5=makeQuery(id+"F3.imprint","IMPRINT",FACE,{"disambiguationData":[TD([[makeQuery(id+"F3.imprint","IMPRINT",EDGE,{"derivedFrom":makeQuery(id+"F1.opExtrude","CAP_EDGE",EDGE,{"disambiguationData":[OSD([sQuery(id+"F0.wireOp",EDGE,"E341")])],"isStart":false})}),1.0]])]});
            var Q6;
            Q6=makeQuery(id+"F3.imprint","IMPRINT",FACE,{"disambiguationData":[TD([[makeQuery(id+"F3.imprint","IMPRINT",EDGE,{"derivedFrom":makeQuery(id+"F1.opExtrude","CAP_EDGE",EDGE,{"disambiguationData":[OSD([sQuery(id+"F0.wireOp",EDGE,"E330")])],"isStart":false})}),1.0]])]});
            var Q7;
            Q7=makeQuery(id+"F3.imprint","IMPRINT",FACE,{"disambiguationData":[TD([[makeQuery(id+"F3.imprint","IMPRINT",EDGE,{"derivedFrom":makeQuery(id+"F1.opExtrude","CAP_EDGE",EDGE,{"disambiguationData":[OSD([sQuery(id+"F0.wireOp",EDGE,"E336")])],"isStart":false})}),1.0]])]});
            var Q8;
            Q8=makeQuery(id+"F3.imprint","IMPRINT",FACE,{"disambiguationData":[TD([[makeQuery(id+"F3.imprint","IMPRINT",EDGE,{"derivedFrom":makeQuery(id+"F1.opExtrude","CAP_EDGE",EDGE,{"disambiguationData":[OSD([sQuery(id+"F0.wireOp",EDGE,"E280")])],"isStart":false})}),1.0]])]});
            var Q9;
            Q9=makeQuery(id+"F3.imprint","IMPRINT",FACE,{"disambiguationData":[TD([[makeQuery(id+"F3.imprint","IMPRINT",EDGE,{"derivedFrom":makeQuery(id+"F1.opExtrude","CAP_EDGE",EDGE,{"disambiguationData":[OSD([sQuery(id+"F0.wireOp",EDGE,"E265")])],"isStart":false})}),1.0]])]});
            var Q10;
            Q10=makeQuery(id+"F3.imprint","IMPRINT",FACE,{"disambiguationData":[TD([[makeQuery(id+"F3.imprint","IMPRINT",EDGE,{"derivedFrom":makeQuery(id+"F1.opExtrude","CAP_EDGE",EDGE,{"disambiguationData":[OSD([sQuery(id+"F0.wireOp",EDGE,"E237")])],"isStart":false})}),1.0]])]});
            var Q11;
            Q11=makeQuery(id+"F3.imprint","IMPRINT",FACE,{"disambiguationData":[TD([[makeQuery(id+"F3.imprint","IMPRINT",EDGE,{"derivedFrom":makeQuery(id+"F1.opExtrude","CAP_EDGE",EDGE,{"disambiguationData":[OSD([sQuery(id+"F0.wireOp",EDGE,"E221")])],"isStart":false})}),1.0]])]});
            var Q12;
            Q12=makeQuery(id+"F3.imprint","IMPRINT",FACE,{"disambiguationData":[TD([[makeQuery(id+"F3.imprint","IMPRINT",EDGE,{"derivedFrom":makeQuery(id+"F1.opExtrude","CAP_EDGE",EDGE,{"disambiguationData":[OSD([sQuery(id+"F0.wireOp",EDGE,"E295")])],"isStart":false})}),1.0]])]});
            var Q13;
            Q13=makeQuery(id+"F3.imprint","IMPRINT",FACE,{"disambiguationData":[TD([[makeQuery(id+"F3.imprint","IMPRINT",EDGE,{"derivedFrom":makeQuery(id+"F1.opExtrude","CAP_EDGE",EDGE,{"disambiguationData":[OSD([sQuery(id+"F0.wireOp",EDGE,"E104")])],"isStart":false})}),-1.0]])]});
            var Q14;
            Q14=makeQuery(id+"F3.imprint","IMPRINT",FACE,{"disambiguationData":[TD([[makeQuery(id+"F3.imprint","IMPRINT",EDGE,{"derivedFrom":makeQuery(id+"F1.opExtrude","CAP_EDGE",EDGE,{"disambiguationData":[OSD([sQuery(id+"F0.wireOp",EDGE,"E100")])],"isStart":false})}),1.0]])]});
            var Q15;
            Q15=makeQuery(id+"F3.imprint","IMPRINT",FACE,{"disambiguationData":[TD([[makeQuery(id+"F3.imprint","IMPRINT",EDGE,{"derivedFrom":makeQuery(id+"F1.opExtrude","CAP_EDGE",EDGE,{"disambiguationData":[OSD([sQuery(id+"F0.wireOp",EDGE,"E112")])],"isStart":false})}),1.0]])]});
            var Q16;
            Q16=makeQuery(id+"F3.imprint","IMPRINT",FACE,{"disambiguationData":[TD([[makeQuery(id+"F3.imprint","IMPRINT",EDGE,{"derivedFrom":makeQuery(id+"F1.opExtrude","CAP_EDGE",EDGE,{"disambiguationData":[OSD([sQuery(id+"F0.wireOp",EDGE,"E96")])],"isStart":false})}),1.0]])]});
            var Q17;
            Q17=makeQuery(id+"F3.imprint","IMPRINT",FACE,{"disambiguationData":[TD([[makeQuery(id+"F3.imprint","IMPRINT",EDGE,{"derivedFrom":makeQuery(id+"F1.opExtrude","CAP_EDGE",EDGE,{"disambiguationData":[OSD([sQuery(id+"F0.wireOp",EDGE,"E92")])],"isStart":false})}),1.0]])]});
            var Q18;
            Q18=makeQuery(id+"F3.imprint","IMPRINT",FACE,{"disambiguationData":[TD([[makeQuery(id+"F3.imprint","IMPRINT",EDGE,{"derivedFrom":makeQuery(id+"F1.opExtrude","CAP_EDGE",EDGE,{"disambiguationData":[OSD([sQuery(id+"F0.wireOp",EDGE,"E88")])],"isStart":false})}),1.0]])]});
            var Q19;
            Q19=makeQuery(id+"F3.imprint","IMPRINT",FACE,{"disambiguationData":[TD([[makeQuery(id+"F3.imprint","IMPRINT",EDGE,{"derivedFrom":makeQuery(id+"F1.opExtrude","CAP_EDGE",EDGE,{"disambiguationData":[OSD([sQuery(id+"F0.wireOp",EDGE,"E140")])],"isStart":false})}),-1.0]])]});
            var Q20;
            Q20=makeQuery(id+"F3.imprint","IMPRINT",FACE,{"disambiguationData":[TD([[makeQuery(id+"F3.imprint","IMPRINT",EDGE,{"derivedFrom":makeQuery(id+"F1.opExtrude","CAP_EDGE",EDGE,{"disambiguationData":[OSD([sQuery(id+"F0.wireOp",EDGE,"E84")])],"isStart":false})}),1.0]])]});
            var Q21;
            Q21=makeQuery(id+"F3.imprint","IMPRINT",FACE,{"disambiguationData":[TD([[makeQuery(id+"F3.imprint","IMPRINT",EDGE,{"derivedFrom":makeQuery(id+"F1.opExtrude","CAP_EDGE",EDGE,{"disambiguationData":[OSD([sQuery(id+"F0.wireOp",EDGE,"E80")])],"isStart":false})}),1.0]])]});
            var Q22;
            Q22=makeQuery(id+"F3.imprint","IMPRINT",FACE,{"disambiguationData":[TD([[makeQuery(id+"F3.imprint","IMPRINT",EDGE,{"derivedFrom":makeQuery(id+"F1.opExtrude","CAP_EDGE",EDGE,{"disambiguationData":[OSD([sQuery(id+"F0.wireOp",EDGE,"E136")])],"isStart":false})}),-1.0]])]});
            var Q23;
            Q23=makeQuery(id+"F3.imprint","IMPRINT",FACE,{"disambiguationData":[TD([[makeQuery(id+"F3.imprint","IMPRINT",EDGE,{"derivedFrom":makeQuery(id+"F1.opExtrude","CAP_EDGE",EDGE,{"disambiguationData":[OSD([sQuery(id+"F0.wireOp",EDGE,"E128")])],"isStart":false})}),1.0]])]});
            var Q24;
            Q24=makeQuery(id+"F3.imprint","IMPRINT",FACE,{"disambiguationData":[TD([[makeQuery(id+"F3.imprint","IMPRINT",EDGE,{"derivedFrom":makeQuery(id+"F1.opExtrude","CAP_EDGE",EDGE,{"disambiguationData":[OSD([sQuery(id+"F0.wireOp",EDGE,"E108")])],"isStart":false})}),1.0]])]});
            var Q25;
            Q25=makeQuery(id+"F3.imprint","IMPRINT",FACE,{"disambiguationData":[TD([[makeQuery(id+"F3.imprint","IMPRINT",EDGE,{"derivedFrom":makeQuery(id+"F1.opExtrude","CAP_EDGE",EDGE,{"disambiguationData":[OSD([sQuery(id+"F0.wireOp",EDGE,"E124")])],"isStart":false})}),1.0]])]});
            var Q26;
            Q26=makeQuery(id+"F3.imprint","IMPRINT",FACE,{"disambiguationData":[TD([[makeQuery(id+"F3.imprint","IMPRINT",EDGE,{"derivedFrom":makeQuery(id+"F1.opExtrude","CAP_EDGE",EDGE,{"disambiguationData":[OSD([sQuery(id+"F0.wireOp",EDGE,"E116")])],"isStart":false})}),-1.0]])]});
            var Q27;
            Q27=makeQuery(id+"F3.imprint","IMPRINT",FACE,{"disambiguationData":[TD([[makeQuery(id+"F3.imprint","IMPRINT",EDGE,{"derivedFrom":makeQuery(id+"F1.opExtrude","CAP_EDGE",EDGE,{"disambiguationData":[OSD([sQuery(id+"F0.wireOp",EDGE,"E8")])],"isStart":false})}),1.0]])]});
            var Q28;
            Q28=makeQuery(id+"F3.imprint","IMPRINT",FACE,{"disambiguationData":[TD([[makeQuery(id+"F3.imprint","IMPRINT",EDGE,{"derivedFrom":makeQuery(id+"F1.opExtrude","CAP_EDGE",EDGE,{"disambiguationData":[OSD([sQuery(id+"F0.wireOp",EDGE,"E4")])],"isStart":false})}),1.0]])]});
            var Q29;
            Q29=makeQuery(id+"F3.imprint","IMPRINT",FACE,{"disambiguationData":[TD([[makeQuery(id+"F3.imprint","IMPRINT",EDGE,{"derivedFrom":makeQuery(id+"F1.opExtrude","CAP_EDGE",EDGE,{"disambiguationData":[OSD([sQuery(id+"F0.wireOp",EDGE,"E0")])],"isStart":false})}),1.0]])]});
            var Q30;
            Q30=makeQuery(id+"F3.imprint","IMPRINT",FACE,{"disambiguationData":[TD([[makeQuery(id+"F3.imprint","IMPRINT",EDGE,{"derivedFrom":makeQuery(id+"F1.opExtrude","CAP_EDGE",EDGE,{"disambiguationData":[OSD([sQuery(id+"F0.wireOp",EDGE,"E12")])],"isStart":false})}),1.0]])]});
            var Q31;
            Q31=makeQuery(id+"F3.imprint","IMPRINT",FACE,{"disambiguationData":[TD([[makeQuery(id+"F3.imprint","IMPRINT",EDGE,{"derivedFrom":makeQuery(id+"F1.opExtrude","CAP_EDGE",EDGE,{"disambiguationData":[OSD([sQuery(id+"F0.wireOp",EDGE,"E16")])],"isStart":false})}),1.0]])]});
            var Q32;
            Q32=makeQuery(id+"F3.imprint","IMPRINT",FACE,{"disambiguationData":[TD([[makeQuery(id+"F3.imprint","IMPRINT",EDGE,{"derivedFrom":makeQuery(id+"F1.opExtrude","CAP_EDGE",EDGE,{"disambiguationData":[OSD([sQuery(id+"F0.wireOp",EDGE,"E24")])],"isStart":false})}),1.0]])]});
            var Q33;
            Q33=makeQuery(id+"F3.imprint","IMPRINT",FACE,{"disambiguationData":[TD([[makeQuery(id+"F3.imprint","IMPRINT",EDGE,{"derivedFrom":makeQuery(id+"F1.opExtrude","CAP_EDGE",EDGE,{"disambiguationData":[OSD([sQuery(id+"F0.wireOp",EDGE,"E36")])],"isStart":false})}),1.0]])]});
            var Q34;
            Q34=makeQuery(id+"F3.imprint","IMPRINT",FACE,{"disambiguationData":[TD([[makeQuery(id+"F3.imprint","IMPRINT",EDGE,{"derivedFrom":makeQuery(id+"F1.opExtrude","CAP_EDGE",EDGE,{"disambiguationData":[OSD([sQuery(id+"F0.wireOp",EDGE,"E32")])],"isStart":false})}),-1.0]])]});
            var Q35;
            Q35=makeQuery(id+"F3.imprint","IMPRINT",FACE,{"disambiguationData":[TD([[makeQuery(id+"F3.imprint","IMPRINT",EDGE,{"derivedFrom":makeQuery(id+"F1.opExtrude","CAP_EDGE",EDGE,{"disambiguationData":[OSD([sQuery(id+"F0.wireOp",EDGE,"E40")])],"isStart":false})}),-1.0]])]});
            var Q36;
            Q36=makeQuery(id+"F3.imprint","IMPRINT",FACE,{"disambiguationData":[TD([[makeQuery(id+"F3.imprint","IMPRINT",EDGE,{"derivedFrom":makeQuery(id+"F1.opExtrude","CAP_EDGE",EDGE,{"disambiguationData":[OSD([sQuery(id+"F0.wireOp",EDGE,"E44")])],"isStart":false})}),-1.0]])]});
            var Q37;
            Q37=makeQuery(id+"F3.imprint","IMPRINT",FACE,{"disambiguationData":[TD([[makeQuery(id+"F3.imprint","IMPRINT",EDGE,{"derivedFrom":makeQuery(id+"F1.opExtrude","CAP_EDGE",EDGE,{"disambiguationData":[OSD([sQuery(id+"F0.wireOp",EDGE,"E28")])],"isStart":false})}),-1.0]])]});
            var Q38;
            Q38=makeQuery(id+"F3.imprint","IMPRINT",FACE,{"disambiguationData":[TD([[makeQuery(id+"F3.imprint","IMPRINT",EDGE,{"derivedFrom":makeQuery(id+"F1.opExtrude","CAP_EDGE",EDGE,{"disambiguationData":[OSD([sQuery(id+"F0.wireOp",EDGE,"E20")])],"isStart":false})}),1.0]])]});
            var Q39;
            Q39=makeQuery(id+"F3.imprint","IMPRINT",FACE,{"disambiguationData":[TD([[makeQuery(id+"F3.imprint","IMPRINT",EDGE,{"derivedFrom":makeQuery(id+"F1.opExtrude","CAP_EDGE",EDGE,{"disambiguationData":[OSD([sQuery(id+"F0.wireOp",EDGE,"E120")])],"isStart":false})}),-1.0]])]});
            var Q40;
            Q40=makeQuery(id+"F3.imprint","IMPRINT",FACE,{"disambiguationData":[TD([[makeQuery(id+"F3.imprint","IMPRINT",EDGE,{"derivedFrom":makeQuery(id+"F1.opExtrude","CAP_EDGE",EDGE,{"disambiguationData":[OSD([sQuery(id+"F0.wireOp",EDGE,"E132")])],"isStart":false})}),-1.0]])]});
            var Q41;
            Q41=makeQuery(id+"F3.imprint","IMPRINT",FACE,{"disambiguationData":[TD([[makeQuery(id+"F3.imprint","IMPRINT",EDGE,{"derivedFrom":makeQuery(id+"F1.opExtrude","CAP_EDGE",EDGE,{"disambiguationData":[OSD([sQuery(id+"F0.wireOp",EDGE,"E144")])],"isStart":false})}),1.0]])]});
            var Q42;
            Q42=makeQuery(id+"F3.imprint","IMPRINT",FACE,{"disambiguationData":[TD([[makeQuery(id+"F3.imprint","IMPRINT",EDGE,{"derivedFrom":makeQuery(id+"F1.opExtrude","CAP_EDGE",EDGE,{"disambiguationData":[OSD([sQuery(id+"F0.wireOp",EDGE,"E148")])],"isStart":false})}),-1.0]])]});
            var Q43;
            Q43=makeQuery(id+"F3.imprint","IMPRINT",FACE,{"disambiguationData":[TD([[makeQuery(id+"F3.imprint","IMPRINT",EDGE,{"derivedFrom":makeQuery(id+"F1.opExtrude","CAP_EDGE",EDGE,{"disambiguationData":[OSD([sQuery(id+"F0.wireOp",EDGE,"E183")])],"isStart":false})}),1.0]])]});
            var Q44;
            Q44=makeQuery(id+"F3.imprint","IMPRINT",FACE,{"disambiguationData":[TD([[makeQuery(id+"F3.imprint","IMPRINT",EDGE,{"derivedFrom":makeQuery(id+"F1.opExtrude","CAP_EDGE",EDGE,{"disambiguationData":[OSD([sQuery(id+"F0.wireOp",EDGE,"E76")])],"isStart":false})}),1.0]])]});
            var Q45;
            Q45=makeQuery(id+"F3.imprint","IMPRINT",FACE,{"disambiguationData":[TD([[makeQuery(id+"F3.imprint","IMPRINT",EDGE,{"derivedFrom":makeQuery(id+"F1.opExtrude","CAP_EDGE",EDGE,{"disambiguationData":[OSD([sQuery(id+"F0.wireOp",EDGE,"E152")])],"isStart":false})}),1.0]])]});
            var Q46;
            Q46=makeQuery(id+"F3.imprint","IMPRINT",FACE,{"disambiguationData":[TD([[makeQuery(id+"F3.imprint","IMPRINT",EDGE,{"derivedFrom":makeQuery(id+"F1.opExtrude","CAP_EDGE",EDGE,{"disambiguationData":[OSD([sQuery(id+"F0.wireOp",EDGE,"E156")])],"isStart":false})}),-1.0]])]});
            var Q47;
            Q47=makeQuery(id+"F3.imprint","IMPRINT",FACE,{"disambiguationData":[TD([[makeQuery(id+"F3.imprint","IMPRINT",EDGE,{"derivedFrom":makeQuery(id+"F1.opExtrude","CAP_EDGE",EDGE,{"disambiguationData":[OSD([sQuery(id+"F0.wireOp",EDGE,"E160")])],"isStart":false})}),1.0]])]});
            var Q48;
            Q48=makeQuery(id+"F3.imprint","IMPRINT",FACE,{"disambiguationData":[TD([[makeQuery(id+"F3.imprint","IMPRINT",EDGE,{"derivedFrom":makeQuery(id+"F1.opExtrude","CAP_EDGE",EDGE,{"disambiguationData":[OSD([sQuery(id+"F0.wireOp",EDGE,"E163")])],"isStart":false})}),-1.0]])]});
            var Q49;
            Q49=makeQuery(id+"F3.imprint","IMPRINT",FACE,{"disambiguationData":[TD([[makeQuery(id+"F3.imprint","IMPRINT",EDGE,{"derivedFrom":makeQuery(id+"F1.opExtrude","CAP_EDGE",EDGE,{"disambiguationData":[OSD([sQuery(id+"F0.wireOp",EDGE,"E167")])],"isStart":false})}),-1.0]])]});
            var Q50;
            Q50=makeQuery(id+"F3.imprint","IMPRINT",FACE,{"disambiguationData":[TD([[makeQuery(id+"F3.imprint","IMPRINT",EDGE,{"derivedFrom":makeQuery(id+"F1.opExtrude","CAP_EDGE",EDGE,{"disambiguationData":[OSD([sQuery(id+"F0.wireOp",EDGE,"E48")])],"isStart":false})}),-1.0]])]});
            var Q51;
            Q51=makeQuery(id+"F3.imprint","IMPRINT",FACE,{"disambiguationData":[TD([[makeQuery(id+"F3.imprint","IMPRINT",EDGE,{"derivedFrom":makeQuery(id+"F1.opExtrude","CAP_EDGE",EDGE,{"disambiguationData":[OSD([sQuery(id+"F0.wireOp",EDGE,"E52")])],"isStart":false})}),-1.0]])]});
            var Q52;
            Q52=makeQuery(id+"F3.imprint","IMPRINT",FACE,{"disambiguationData":[TD([[makeQuery(id+"F3.imprint","IMPRINT",EDGE,{"derivedFrom":makeQuery(id+"F1.opExtrude","CAP_EDGE",EDGE,{"disambiguationData":[OSD([sQuery(id+"F0.wireOp",EDGE,"E56")])],"isStart":false})}),1.0]])]});
            var Q53;
            Q53=makeQuery(id+"F3.imprint","IMPRINT",FACE,{"disambiguationData":[TD([[makeQuery(id+"F3.imprint","IMPRINT",EDGE,{"derivedFrom":makeQuery(id+"F1.opExtrude","CAP_EDGE",EDGE,{"disambiguationData":[OSD([sQuery(id+"F0.wireOp",EDGE,"E61")])],"isStart":false})}),1.0]])]});
            var Q54;
            Q54=makeQuery(id+"F3.imprint","IMPRINT",FACE,{"disambiguationData":[TD([[makeQuery(id+"F3.imprint","IMPRINT",EDGE,{"derivedFrom":makeQuery(id+"F1.opExtrude","CAP_EDGE",EDGE,{"disambiguationData":[OSD([sQuery(id+"F0.wireOp",EDGE,"E69")])],"isStart":false})}),1.0]])]});
            var Q55;
            Q55=makeQuery(id+"F3.imprint","IMPRINT",FACE,{"disambiguationData":[TD([[makeQuery(id+"F3.imprint","IMPRINT",EDGE,{"derivedFrom":makeQuery(id+"F1.opExtrude","CAP_EDGE",EDGE,{"disambiguationData":[OSD([sQuery(id+"F0.wireOp",EDGE,"E65")])],"isStart":false})}),1.0]])]});
            var Q56;
            Q56=makeQuery(id+"F3.imprint","IMPRINT",FACE,{"disambiguationData":[TD([[makeQuery(id+"F3.imprint","IMPRINT",EDGE,{"derivedFrom":makeQuery(id+"F1.opExtrude","CAP_EDGE",EDGE,{"disambiguationData":[OSD([sQuery(id+"F0.wireOp",EDGE,"E72")])],"isStart":false})}),1.0]])]});
            var Q57;
            Q57=makeQuery(id+"F3.imprint","IMPRINT",FACE,{"disambiguationData":[TD([[makeQuery(id+"F3.imprint","IMPRINT",EDGE,{"derivedFrom":makeQuery(id+"F1.opExtrude","CAP_EDGE",EDGE,{"disambiguationData":[OSD([sQuery(id+"F0.wireOp",EDGE,"E179")])],"isStart":false})}),-1.0]])]});
            var Q58;
            Q58=makeQuery(id+"F3.imprint","IMPRINT",FACE,{"disambiguationData":[TD([[makeQuery(id+"F3.imprint","IMPRINT",EDGE,{"derivedFrom":makeQuery(id+"F1.opExtrude","CAP_EDGE",EDGE,{"disambiguationData":[OSD([sQuery(id+"F0.wireOp",EDGE,"E175")])],"isStart":false})}),-1.0]])]});
            var Q59;
            Q59=makeQuery(id+"F3.imprint","IMPRINT",FACE,{"disambiguationData":[TD([[makeQuery(id+"F3.imprint","IMPRINT",EDGE,{"derivedFrom":makeQuery(id+"F1.opExtrude","CAP_EDGE",EDGE,{"disambiguationData":[OSD([sQuery(id+"F0.wireOp",EDGE,"E171")])],"isStart":false})}),-1.0]])]});
            extrude(context, id + "F4", {"entities" : qUnion([Q0, Q1, Q2, Q3, Q4, Q5, Q6, Q7, Q8, Q9, Q10, Q11, Q12, Q13, Q14, Q15, Q16, Q17, Q18, Q19, Q20, Q21, Q22, Q23, Q24, Q25, Q26, Q27, Q28, Q29, Q30, Q31, Q32, Q33, Q34, Q35, Q36, Q37, Q38, Q39, Q40, Q41, Q42, Q43, Q44, Q45, Q46, Q47, Q48, Q49, Q50, Q51, Q52, Q53, Q54, Q55, Q56, Q57, Q58, Q59]), "depth" : 5.08 * mm, "offsetDistance" : 25.4 * mm, "hasSecondDirection" : true, "secondDirectionOppositeDirection" : true, "secondDirectionDepth" : 7.62 * mm});
        }
    });
